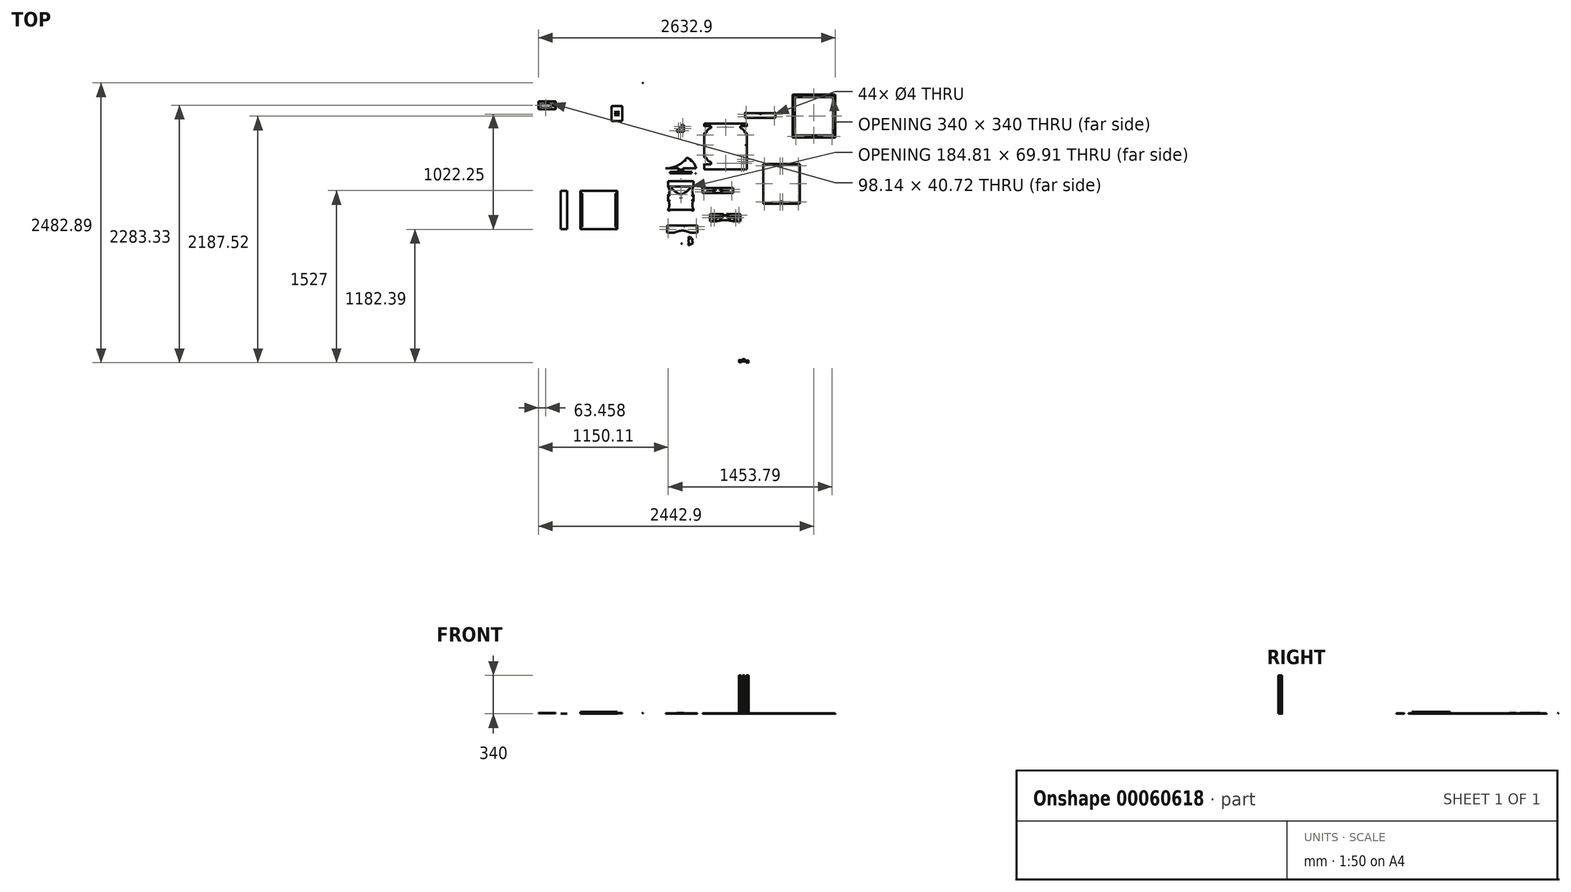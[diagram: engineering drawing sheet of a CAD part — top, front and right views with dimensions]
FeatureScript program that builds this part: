
annotation { "Feature Type Name" : "Feature", "Feature Type Description" : "" }
export const myFeature = defineFeature(function(context is Context, id is Id, definition is map)
    precondition{}
    {
        {
            var Q0;
            Q0=qCreatedBy(makeId("Top.planeOp"),FACE);
            var sketch = newSketch(context, id + "F0", { "sketchPlane" : qUnion([Q0])});
            skLineSegment(sketch, "E0", {"start": v(-196.4, -19.93) * mm, "end": v(-196.4, 30.07) * mm});
            skCircle(sketch, "E1", {"center": v(-187.75, 27.57) * mm, "radius": 2.75 * mm});
            skCircle(sketch, "E2", {"center": v(-187.75, -17.43) * mm, "radius": 2.75 * mm});
            skArc(sketch, "E3", {"start": v(-196.4, -19.93) * mm, "mid": v(-194.93, -23.47) * mm, "end": v(-191.4, -24.93) * mm});
            skArc(sketch, "E4", {"start": v(-191.4, 35.07) * mm, "mid": v(-194.93, 33.6) * mm, "end": v(-196.4, 30.07) * mm});
            skLineSegment(sketch, "E5", {"start": v(28.6, 30.07) * mm, "end": v(28.6, -19.93) * mm});
            skCircle(sketch, "E6", {"center": v(19.95, 27.57) * mm, "radius": 5.08 * mm});
            skCircle(sketch, "E7", {"center": v(19.95, -17.43) * mm, "radius": 5.08 * mm});
            skLineSegment(sketch, "E8.trimOffspring", {"start": v(14.88, 27.57) * mm, "end": v(19.95, 27.57) * mm});
            skPoint(sketch, "E9.visualSharp", {"position": v(28.6, 35.07) * mm});
            skArc(sketch, "E9.filletArc", {"start": v(28.6, 30.07) * mm, "mid": v(27.14, 33.6) * mm, "end": v(23.6, 35.07) * mm});
            skPoint(sketch, "E10.visualSharp", {"position": v(28.6, -24.93) * mm});
            skArc(sketch, "E10.filletArc", {"start": v(23.6, -24.93) * mm, "mid": v(27.14, -23.47) * mm, "end": v(28.6, -19.93) * mm});
            skCircle(sketch, "E11", {"center": v(-83.9, 5.07) * mm, "radius": 3.2 * mm});
            skLineSegment(sketch, "E12", {"start": v(-87.4, 19.55) * mm, "end": v(-80.33, 19.55) * mm});
            skLineSegment(sketch, "E13", {"start": v(-87.4, 21.55) * mm, "end": v(-80.33, 21.55) * mm});
            skLineSegment(sketch, "E14", {"start": v(-87.4, 23.86) * mm, "end": v(-80.32, 23.86) * mm});
            skLineSegment(sketch, "E15", {"start": v(-87.4, 25.86) * mm, "end": v(-80.32, 25.86) * mm});
            skLineSegment(sketch, "E16", {"start": v(-87.4, 27.93) * mm, "end": v(-80.32, 27.92) * mm});
            skLineSegment(sketch, "E17", {"start": v(-87.4, 31.34) * mm, "end": v(-80.31, 31.33) * mm});
            skLineSegment(sketch, "E18", {"start": v(-87.4, -9.95) * mm, "end": v(-80.38, -9.95) * mm});
            skLineSegment(sketch, "E19", {"start": v(-87.4, -11.95) * mm, "end": v(-80.38, -11.95) * mm});
            skLineSegment(sketch, "E20", {"start": v(-87.4, -16.14) * mm, "end": v(-80.39, -16.14) * mm});
            skLineSegment(sketch, "E21", {"start": v(-87.4, -14.14) * mm, "end": v(-80.39, -14.14) * mm});
            skLineSegment(sketch, "E22", {"start": v(-87.4, -21.89) * mm, "end": v(-80.4, -21.89) * mm});
            skLineSegment(sketch, "E23", {"start": v(-87.4, -18.45) * mm, "end": v(-80.4, -18.45) * mm});
            skLineSegment(sketch, "E24", {"start": v(-83.9, -21.89) * mm, "end": v(-80.4, -21.89) * mm});
            skLineSegment(sketch, "E25", {"start": v(-83.9, -21.89) * mm, "end": v(-87.4, -21.89) * mm});
            skLineSegment(sketch, "E26", {"start": v(-87.4, -21.89) * mm, "end": v(-87.4, -18.45) * mm});
            skLineSegment(sketch, "E27", {"start": v(-80.4, -21.89) * mm, "end": v(-80.4, -18.45) * mm});
            skLineSegment(sketch, "E28.trimOffspring", {"start": v(-87.4, 19.55) * mm, "end": v(-87.4, 21.55) * mm});
            skLineSegment(sketch, "E29.trimOffspring", {"start": v(-80.33, 19.55) * mm, "end": v(-80.33, 21.55) * mm});
            skLineSegment(sketch, "E30.trimOffspring", {"start": v(-80.32, 27.92) * mm, "end": v(-80.31, 31.34) * mm});
            skLineSegment(sketch, "E31.trimOffspring", {"start": v(-87.4, 27.93) * mm, "end": v(-87.4, 31.34) * mm});
            skLineSegment(sketch, "E32.trimOffspring", {"start": v(-87.4, 23.86) * mm, "end": v(-87.4, 25.86) * mm});
            skLineSegment(sketch, "E33.trimOffspring", {"start": v(-80.32, 23.86) * mm, "end": v(-80.32, 25.86) * mm});
            skLineSegment(sketch, "E34.trimOffspring", {"start": v(-87.4, -16.14) * mm, "end": v(-87.4, -14.14) * mm});
            skPoint(sketch, "E35.trimOffspring.end.orphan", {"position": v(-83.9, -24.93) * mm});
            skLineSegment(sketch, "E36.trimOffspring", {"start": v(-80.39, -16.14) * mm, "end": v(-80.39, -14.14) * mm});
            skLineSegment(sketch, "E37.trimOffspring", {"start": v(-87.4, -11.95) * mm, "end": v(-87.4, -9.95) * mm});
            skLineSegment(sketch, "E38.trimOffspring", {"start": v(-80.38, -11.95) * mm, "end": v(-80.38, -9.95) * mm});
            skCircle(sketch, "E39", {"center": v(-188.4, 109.57) * mm, "radius": 1.5 * mm});
            skCircle(sketch, "E40", {"center": v(20.6, 109.57) * mm, "radius": 1.5 * mm});
            skCircle(sketch, "E41", {"center": v(-188.4, -99.43) * mm, "radius": 1.5 * mm});
            skCircle(sketch, "E42", {"center": v(20.6, -99.43) * mm, "radius": 1.5 * mm});
            skLineSegment(sketch, "E43.MirrorCS", {"start": v(28.6, -19.93) * mm, "end": v(28.6, 30.07) * mm});
            skArc(sketch, "E44", {"start": v(-196.14, -94.85) * mm, "mid": v(-190.78, -108.11) * mm, "end": v(-179.4, -99.43) * mm});
            skArc(sketch, "E45", {"start": v(11.6, -99.43) * mm, "mid": v(22.98, -108.11) * mm, "end": v(28.34, -94.85) * mm});
            skArc(sketch, "E46", {"start": v(28.34, 104.98) * mm, "mid": v(22.98, 118.25) * mm, "end": v(11.6, 109.57) * mm});
            skArc(sketch, "E47", {"start": v(-179.4, 109.57) * mm, "mid": v(-190.78, 118.25) * mm, "end": v(-196.14, 104.98) * mm});
            skArc(sketch, "E48", {"start": v(-196.14, -94.85) * mm, "mid": v(-185.98, -60.42) * mm, "end": v(-191.4, -24.93) * mm});
            skArc(sketch, "E49", {"start": v(-83.9, -24.93) * mm, "mid": v(-137.85, -54.24) * mm, "end": v(-179.4, -99.43) * mm});
            skArc(sketch, "E50.MirrorCS", {"start": v(-83.9, -24.93) * mm, "mid": v(-29.95, -54.24) * mm, "end": v(11.6, -99.43) * mm});
            skArc(sketch, "E51.MirrorCS", {"start": v(28.34, -94.85) * mm, "mid": v(18.18, -60.42) * mm, "end": v(23.6, -24.93) * mm});
            skArc(sketch, "E52.MirrorCS", {"start": v(-83.9, 35.07) * mm, "mid": v(-137.85, 64.37) * mm, "end": v(-179.4, 109.57) * mm});
            skArc(sketch, "E53.MirrorCS", {"start": v(-196.14, 104.98) * mm, "mid": v(-185.98, 70.55) * mm, "end": v(-191.4, 35.07) * mm});
            skArc(sketch, "E54.MirrorCS", {"start": v(-83.9, 35.07) * mm, "mid": v(-29.95, 64.37) * mm, "end": v(11.6, 109.57) * mm});
            skArc(sketch, "E55.MirrorCS", {"start": v(28.34, 104.98) * mm, "mid": v(18.18, 70.55) * mm, "end": v(23.6, 35.07) * mm});
            skLineSegment(sketch, "E56.trimOffspring", {"start": v(-196.4, 5.07) * mm, "end": v(-227.61, 5.07) * mm});
            skLineSegment(sketch, "E57", {"start": v(-179.4, -99.43) * mm, "end": v(11.6, -99.43) * mm});
            skLineSegment(sketch, "E58", {"start": v(-179.4, 109.57) * mm, "end": v(11.6, 109.57) * mm});
            skLineSegment(sketch, "E59.bottom", {"start": v(-196.14, 104.98) * mm, "end": v(28.34, 104.98) * mm});
            skLineSegment(sketch, "E59.top", {"start": v(-196.14, 155.03) * mm, "end": v(28.34, 155.03) * mm});
            skLineSegment(sketch, "E59.left", {"start": v(-196.14, 104.98) * mm, "end": v(-196.14, 155.03) * mm});
            skLineSegment(sketch, "E59.right", {"start": v(28.34, 104.98) * mm, "end": v(28.34, 155.03) * mm});
            skSolve(sketch);
        }
        {
            var Q0;
            Q0=makeQuery(id+"F0.imprint","IMPRINT",FACE,{"disambiguationData":[TD([[makeQuery(id+"F0.imprint","IMPRINT",EDGE,{"derivedFrom":sQuery(id+"F0.wireOp",EDGE,"E0")}),-1.0]])]});
            var Q1;
            Q1=makeQuery(id+"F0.imprint","IMPRINT",FACE,{"disambiguationData":[TD([[makeQuery(id+"F0.imprint","IMPRINT",EDGE,{"derivedFrom":sQuery(id+"F0.wireOp",EDGE,"E23")}),-1.0]])]});
            var Q2;
            Q2=makeQuery(id+"F0.imprint","IMPRINT",FACE,{"disambiguationData":[TD([[makeQuery(id+"F0.imprint","IMPRINT",EDGE,{"derivedFrom":sQuery(id+"F0.wireOp",EDGE,"E49")}),1.0]])]});
            var Q3;
            Q3=makeQuery(id+"F0.imprint","IMPRINT",FACE,{"disambiguationData":[TD([[makeQuery(id+"F0.imprint","IMPRINT",EDGE,{"derivedFrom":sQuery(id+"F0.wireOp",EDGE,"E18")}),-1.0]])]});
            var Q4;
            Q4=makeQuery(id+"F0.imprint","IMPRINT",FACE,{"disambiguationData":[TD([[makeQuery(id+"F0.imprint","IMPRINT",EDGE,{"derivedFrom":sQuery(id+"F0.wireOp",EDGE,"E20")}),1.0]])]});
            var Q5;
            Q5=makeQuery(id+"F0.imprint","IMPRINT",FACE,{"disambiguationData":[TD([[makeQuery(id+"F0.imprint","IMPRINT",EDGE,{"derivedFrom":sQuery(id+"F0.wireOp",EDGE,"E52.MirrorCS")}),-1.0]])]});
            var Q6;
            Q6=makeQuery(id+"F0.imprint","IMPRINT",FACE,{"disambiguationData":[TD([[makeQuery(id+"F0.imprint","IMPRINT",EDGE,{"derivedFrom":sQuery(id+"F0.wireOp",EDGE,"E12")}),1.0]])]});
            var Q7;
            Q7=makeQuery(id+"F0.imprint","IMPRINT",FACE,{"disambiguationData":[TD([[makeQuery(id+"F0.imprint","IMPRINT",EDGE,{"derivedFrom":sQuery(id+"F0.wireOp",EDGE,"E14")}),1.0]])]});
            var Q8;
            {var subQ2=sQuery(id+"F0.wireOp",EDGE,"E16");Q8=makeQuery(id+"F0.imprint","IMPRINT",FACE,{"disambiguationData":[TD([[makeQuery(id+"F0.imprint","IMPRINT",EDGE,{"derivedFrom":subQ2}),1.0]])]});}
            var Q9;
            {var subQ7=sQuery(id+"F0.wireOp",EDGE,"E58");Q9=makeQuery(id+"F0.imprint","IMPRINT",FACE,{"disambiguationData":[TD([[makeQuery(id+"F0.imprint","IMPRINT",EDGE,{"derivedFrom":subQ7}),1.0]])]});}
            var Q10;
            Q10=makeQuery(id+"F0.imprint","IMPRINT",FACE,{"disambiguationData":[TD([[makeQuery(id+"F0.imprint","IMPRINT",EDGE,{"derivedFrom":sQuery(id+"F0.wireOp",EDGE,"E40")}),-1.0]])]});
            var Q11;
            Q11=makeQuery(id+"F0.imprint","IMPRINT",FACE,{"disambiguationData":[TD([[makeQuery(id+"F0.imprint","IMPRINT",EDGE,{"derivedFrom":sQuery(id+"F0.wireOp",EDGE,"E39")}),-1.0]])]});
            var Q12;
            {var subQ5=sQuery(id+"F0.wireOp",EDGE,"E58");Q12=makeQuery(id+"F0.imprint","IMPRINT",FACE,{"disambiguationData":[TD([[makeQuery(id+"F0.imprint","IMPRINT",EDGE,{"derivedFrom":subQ5}),-1.0]])]});}
            extrude(context, id + "F1", {"entities" : qUnion([Q0, Q1, Q2, Q3, Q4, Q5, Q6, Q7, Q8, Q9, Q10, Q11, Q12]), "depth" : 4 * mm});
        }
        {
            var Q0;
            Q0=qCreatedBy(makeId("Top.planeOp"),FACE);
            var sketch = newSketch(context, id + "F2", { "sketchPlane" : qUnion([Q0])});
            skLineSegment(sketch, "E60", {"start": v(-104.69, 266.67) * mm, "end": v(-62.63, 266.67) * mm});
            skLineSegment(sketch, "E61", {"start": v(-62.63, 266.67) * mm, "end": v(-62.63, 266.67) * mm});
            skLineSegment(sketch, "E62", {"start": v(-62.63, 266.67) * mm, "end": v(51.38, 266.67) * mm});
            skLineSegment(sketch, "E63", {"start": v(51.38, 266.67) * mm, "end": v(51.38, 224.88) * mm});
            skLineSegment(sketch, "E64", {"start": v(51.38, 224.88) * mm, "end": v(41.38, 224.88) * mm});
            skLineSegment(sketch, "E65", {"start": v(41.38, 224.88) * mm, "end": v(51.38, 224.88) * mm});
            skLineSegment(sketch, "E66.bottom", {"start": v(-104.69, 266.67) * mm, "end": v(-62.62, 266.67) * mm});
            skLineSegment(sketch, "E66.right", {"start": v(-62.62, 266.67) * mm, "end": v(-62.62, 224.88) * mm});
            skLineSegment(sketch, "E67", {"start": v(-104.69, 224.88) * mm, "end": v(-62.62, 224.88) * mm});
            skLineSegment(sketch, "E68", {"start": v(-62.62, 224.88) * mm, "end": v(41.38, 224.88) * mm});
            skLineSegment(sketch, "E69", {"start": v(-104.69, 224.88) * mm, "end": v(-104.69, 266.67) * mm});
            skCircle(sketch, "E70", {"center": v(41.38, 258.88) * mm, "radius": 2 * mm});
            skCircle(sketch, "E71", {"center": v(41.38, 234.88) * mm, "radius": 2 * mm});
            skCircle(sketch, "E72", {"center": v(-83.65, 245.28) * mm, "radius": 11.05 * mm});
            skCircle(sketch, "E73", {"center": v(-99.2, 229.73) * mm, "radius": 1.65 * mm});
            skCircle(sketch, "E74", {"center": v(-68.1, 229.79) * mm, "radius": 1.65 * mm});
            skCircle(sketch, "E75", {"center": v(-99.2, 260.83) * mm, "radius": 1.65 * mm});
            skCircle(sketch, "E76", {"center": v(-68.1, 261) * mm, "radius": 1.65 * mm});
            skLineSegment(sketch, "E77", {"start": v(-83.66, 224.88) * mm, "end": v(-83.66, 266.67) * mm});
            skLineSegment(sketch, "E78.MirrorCS", {"start": v(-104.69, 224.88) * mm, "end": v(-208.69, 224.88) * mm});
            skLineSegment(sketch, "E79.MirrorCS", {"start": v(-104.69, 266.67) * mm, "end": v(-218.69, 266.67) * mm});
            skLineSegment(sketch, "E80.MirrorCS", {"start": v(-218.69, 266.67) * mm, "end": v(-218.69, 224.88) * mm});
            skLineSegment(sketch, "E81.MirrorCS", {"start": v(-208.69, 224.88) * mm, "end": v(-210.69, 224.88) * mm});
            skCircle(sketch, "E82.MirrorC", {"center": v(-208.69, 234.88) * mm, "radius": 2 * mm});
            skCircle(sketch, "E83.MirrorC", {"center": v(-208.69, 258.88) * mm, "radius": 2 * mm});
            skLineSegment(sketch, "E84.bottom", {"start": v(-83.66, 224.88) * mm, "end": v(-181, 224.88) * mm});
            skLineSegment(sketch, "E84.top", {"start": v(-83.66, 237.25) * mm, "end": v(-181, 237.25) * mm});
            skLineSegment(sketch, "E84.left", {"start": v(-83.66, 224.88) * mm, "end": v(-83.66, 237.25) * mm});
            skLineSegment(sketch, "E84.right", {"start": v(-181, 224.88) * mm, "end": v(-181, 237.25) * mm});
            skLineSegment(sketch, "E85.MirrorCS", {"start": v(-83.66, 237.25) * mm, "end": v(13.7, 237.25) * mm});
            skLineSegment(sketch, "E86.MirrorCS", {"start": v(13.7, 224.88) * mm, "end": v(13.7, 237.25) * mm});
            skCircle(sketch, "E87", {"center": v(3.35, 260.88) * mm, "radius": 1.5 * mm});
            skCircle(sketch, "E88", {"center": v(-44.47, 253.5) * mm, "radius": 1.5 * mm});
            skCircle(sketch, "E89", {"center": v(-44.78, 334.21) * mm, "radius": 1.5 * mm});
            skCircle(sketch, "E90", {"center": v(3.26, 334.22) * mm, "radius": 1.5 * mm});
            skArc(sketch, "E91", {"start": v(51.38, 266.67) * mm, "mid": v(26.53, 319.96) * mm, "end": v(-18.2, 358.13) * mm});
            skArc(sketch, "E92", {"start": v(-218.69, 266.67) * mm, "mid": v(-117.85, 289.71) * mm, "end": v(-37.02, 354.25) * mm});
            skArc(sketch, "E93.filletArc", {"start": v(-18.2, 358.13) * mm, "mid": v(-28.3, 359.6) * mm, "end": v(-37.02, 354.25) * mm});
            skLineSegment(sketch, "E94", {"start": v(-218.69, 224.88) * mm, "end": v(-218.69, 220.88) * mm});
            skLineSegment(sketch, "E95", {"start": v(-218.69, 220.88) * mm, "end": v(-210.69, 220.88) * mm});
            skLineSegment(sketch, "E96", {"start": v(-210.69, 220.88) * mm, "end": v(-210.69, 224.88) * mm});
            skLineSegment(sketch, "E97.MirrorCS", {"start": v(51.38, 224.88) * mm, "end": v(51.38, 220.88) * mm});
            skLineSegment(sketch, "E98.MirrorCS", {"start": v(43.38, 220.88) * mm, "end": v(43.38, 224.88) * mm});
            skLineSegment(sketch, "E99.MirrorCS", {"start": v(51.38, 220.88) * mm, "end": v(43.38, 220.88) * mm});
            skPoint(sketch, "E100.orphan", {"position": v(-218.69, 224.88) * mm});
            skSolve(sketch);
        }
        {
            var Q0;
            {var subQ8=sQuery(id+"F2.wireOp",EDGE,"E62");Q0=makeQuery(id+"F2.imprint","IMPRINT",FACE,{"disambiguationData":[TD([[makeQuery(id+"F2.imprint","IMPRINT",EDGE,{"derivedFrom":subQ8}),1.0]])]});}
            var Q1;
            Q1=makeQuery(id+"F2.imprint","IMPRINT",FACE,{"disambiguationData":[TD([[makeQuery(id+"F2.imprint","IMPRINT",EDGE,{"derivedFrom":sQuery(id+"F2.wireOp",EDGE,"E78.MirrorCS")}),-1.0]])]});
            var Q2;
            Q2=makeQuery(id+"F2.imprint","IMPRINT",FACE,{"disambiguationData":[TD([[makeQuery(id+"F2.imprint","IMPRINT",EDGE,{"derivedFrom":sQuery(id+"F2.wireOp",EDGE,"E73")}),-1.0]])]});
            var Q3;
            Q3=makeQuery(id+"F2.imprint","IMPRINT",FACE,{"disambiguationData":[TD([[makeQuery(id+"F2.imprint","IMPRINT",EDGE,{"derivedFrom":sQuery(id+"F2.wireOp",EDGE,"E74")}),-1.0]])]});
            var Q4;
            {var subQ1=sQuery(id+"F2.wireOp",EDGE,"E97.MirrorCS");Q4=makeQuery(id+"F2.imprint","IMPRINT",FACE,{"disambiguationData":[TD([[makeQuery(id+"F2.imprint","IMPRINT",EDGE,{"derivedFrom":subQ1}),-1.0]])]});}
            var Q5;
            Q5=makeQuery(id+"F2.imprint","IMPRINT",FACE,{"disambiguationData":[TD([[makeQuery(id+"F2.imprint","IMPRINT",EDGE,{"derivedFrom":sQuery(id+"F2.wireOp",EDGE,"E75")}),-1.0]])]});
            var Q6;
            Q6=makeQuery(id+"F2.imprint","IMPRINT",FACE,{"disambiguationData":[TD([[makeQuery(id+"F2.imprint","IMPRINT",EDGE,{"derivedFrom":sQuery(id+"F2.wireOp",EDGE,"E76")}),-1.0]])]});
            var Q7;
            {var subQ5=sQuery(id+"F2.wireOp",EDGE,"E86.MirrorCS");Q7=makeQuery(id+"F2.imprint","IMPRINT",FACE,{"disambiguationData":[TD([[makeQuery(id+"F2.imprint","IMPRINT",EDGE,{"derivedFrom":subQ5}),1.0]])]});}
            var Q8;
            {var subQ5=sQuery(id+"F2.wireOp",EDGE,"E84.right");Q8=makeQuery(id+"F2.imprint","IMPRINT",FACE,{"disambiguationData":[TD([[makeQuery(id+"F2.imprint","IMPRINT",EDGE,{"derivedFrom":subQ5}),-1.0]])]});}
            var Q9;
            {var subQ7=sQuery(id+"F2.wireOp",EDGE,"E62");Q9=makeQuery(id+"F2.imprint","IMPRINT",FACE,{"disambiguationData":[TD([[makeQuery(id+"F2.imprint","IMPRINT",EDGE,{"derivedFrom":subQ7}),-1.0]])]});}
            extrude(context, id + "F3", {"entities" : qUnion([Q0, Q1, Q2, Q3, Q4, Q5, Q6, Q7, Q8, Q9]), "depth" : 4 * mm});
        }
        {
            var Q0;
            Q0=qCreatedBy(makeId("Top.planeOp"),FACE);
            var sketch = newSketch(context, id + "F4", { "sketchPlane" : qUnion([Q0])});
            skLineSegment(sketch, "E101", {"start": v(600.2, 758.38) * mm, "end": v(642.2, 758.38) * mm});
            skLineSegment(sketch, "E102", {"start": v(642.2, 758.38) * mm, "end": v(642.2, 758.38) * mm});
            skLineSegment(sketch, "E103", {"start": v(642.2, 758.38) * mm, "end": v(748.23, 758.38) * mm});
            skLineSegment(sketch, "E104", {"start": v(756.23, 758.38) * mm, "end": v(756.23, 716.59) * mm});
            skLineSegment(sketch, "E105", {"start": v(756.23, 716.59) * mm, "end": v(746.23, 716.59) * mm});
            skLineSegment(sketch, "E106", {"start": v(746.23, 716.59) * mm, "end": v(756.23, 716.59) * mm});
            skLineSegment(sketch, "E107.bottom", {"start": v(600.2, 758.38) * mm, "end": v(642.26, 758.38) * mm});
            skLineSegment(sketch, "E107.right", {"start": v(642.26, 758.38) * mm, "end": v(642.26, 716.59) * mm});
            skLineSegment(sketch, "E108", {"start": v(600.2, 716.59) * mm, "end": v(642.26, 716.59) * mm});
            skLineSegment(sketch, "E109", {"start": v(642.26, 716.59) * mm, "end": v(746.23, 716.59) * mm});
            skLineSegment(sketch, "E110", {"start": v(600.2, 716.59) * mm, "end": v(600.2, 758.38) * mm});
            skCircle(sketch, "E111", {"center": v(746.23, 747.66) * mm, "radius": 2 * mm});
            skCircle(sketch, "E112", {"center": v(746.23, 725.6) * mm, "radius": 2 * mm});
            skLineSegment(sketch, "E113", {"start": v(621.23, 716.59) * mm, "end": v(621.23, 758.38) * mm});
            skLineSegment(sketch, "E114.MirrorCS", {"start": v(600.2, 716.59) * mm, "end": v(496.23, 716.59) * mm});
            skLineSegment(sketch, "E115.MirrorCS", {"start": v(600.26, 758.38) * mm, "end": v(494.23, 758.38) * mm});
            skLineSegment(sketch, "E116.MirrorCS", {"start": v(486.23, 758.38) * mm, "end": v(486.23, 716.59) * mm});
            skLineSegment(sketch, "E117.MirrorCS", {"start": v(496.23, 716.59) * mm, "end": v(486.23, 716.59) * mm});
            skCircle(sketch, "E118.MirrorC", {"center": v(496.23, 725.6) * mm, "radius": 2 * mm});
            skCircle(sketch, "E119.MirrorC", {"center": v(496.23, 747.66) * mm, "radius": 2 * mm});
            skCircle(sketch, "E120", {"center": v(621.23, 746.98) * mm, "radius": 1.5 * mm});
            skPoint(sketch, "E121", {"position": v(494.23, 758.38) * mm});
            skPoint(sketch, "E122", {"position": v(735, 758.38) * mm});
            skLineSegment(sketch, "E123", {"start": v(486.23, 758.38) * mm, "end": v(486.23, 762.38) * mm});
            skLineSegment(sketch, "E124", {"start": v(486.23, 762.38) * mm, "end": v(494.23, 762.38) * mm});
            skLineSegment(sketch, "E125", {"start": v(494.23, 762.38) * mm, "end": v(494.23, 758.38) * mm});
            skLineSegment(sketch, "E126.MirrorCS", {"start": v(756.23, 762.38) * mm, "end": v(748.23, 762.38) * mm});
            skLineSegment(sketch, "E127.MirrorCS", {"start": v(756.23, 758.38) * mm, "end": v(756.23, 762.38) * mm});
            skLineSegment(sketch, "E128.MirrorCS", {"start": v(748.23, 762.38) * mm, "end": v(748.23, 758.38) * mm});
            skSolve(sketch);
        }
        {
            var Q0;
            Q0=makeQuery(id+"F4.imprint","IMPRINT",FACE,{"disambiguationData":[TD([[makeQuery(id+"F4.imprint","IMPRINT",EDGE,{"derivedFrom":sQuery(id+"F4.wireOp",EDGE,"E103")}),-1.0]])]});
            var Q1;
            {var subQ8=sQuery(id+"F4.wireOp",EDGE,"E107.right");Q1=makeQuery(id+"F4.imprint","IMPRINT",FACE,{"disambiguationData":[TD([[makeQuery(id+"F4.imprint","IMPRINT",EDGE,{"derivedFrom":subQ8}),-1.0]])]});}
            var Q2;
            {var subQ5=sQuery(id+"F4.wireOp",EDGE,"E110");Q2=makeQuery(id+"F4.imprint","IMPRINT",FACE,{"disambiguationData":[TD([[makeQuery(id+"F4.imprint","IMPRINT",EDGE,{"derivedFrom":subQ5}),-1.0]])]});}
            var Q3;
            {var subQ2=sQuery(id+"F4.wireOp",EDGE,"E110");Q3=makeQuery(id+"F4.imprint","IMPRINT",FACE,{"disambiguationData":[TD([[makeQuery(id+"F4.imprint","IMPRINT",EDGE,{"derivedFrom":subQ2}),1.0]])]});}
            extrude(context, id + "F5", {"entities" : qUnion([Q0, Q1, Q2, Q3]), "depth" : 4 * mm});
        }
        {
            var Q0;
            Q0=qCreatedBy(makeId("Top.planeOp"),FACE);
            var sketch = newSketch(context, id + "F6", { "sketchPlane" : qUnion([Q0])});
            skLineSegment(sketch, "E129", {"start": v(63.81, -240.59) * mm, "end": v(63.81, -260.59) * mm});
            skCircle(sketch, "E130", {"center": v(53.81, -250.59) * mm, "radius": 2 * mm});
            skCircle(sketch, "E131.MirrorC", {"center": v(-196.26, -250.59) * mm, "radius": 2 * mm});
            skCircle(sketch, "E132", {"center": v(-196.26, -274.59) * mm, "radius": 2 * mm});
            skCircle(sketch, "E133.MirrorC", {"center": v(53.81, -274.59) * mm, "radius": 2 * mm});
            skCircle(sketch, "E134", {"center": v(-76.65, -399.92) * mm, "radius": 1.75 * mm});
            skCircle(sketch, "E135", {"center": v(-76.65, -349.92) * mm, "radius": 1.75 * mm});
            skCircle(sketch, "E136", {"center": v(-221.83, -399.92) * mm, "radius": 1.75 * mm});
            skCircle(sketch, "E137", {"center": v(-221.65, -349.97) * mm, "radius": 1.75 * mm});
            skPoint(sketch, "E138", {"position": v(63.81, -264.59) * mm});
            skLineSegment(sketch, "E139", {"start": v(63.81, -264.59) * mm, "end": v(55.81, -264.59) * mm});
            skLineSegment(sketch, "E140", {"start": v(55.81, -264.59) * mm, "end": v(55.81, -260.59) * mm});
            skLineSegment(sketch, "E141", {"start": v(55.81, -260.59) * mm, "end": v(63.81, -260.59) * mm});
            skLineSegment(sketch, "E142.MirrorCS", {"start": v(-206.26, -264.59) * mm, "end": v(-198.26, -264.59) * mm});
            skLineSegment(sketch, "E143.MirrorCS", {"start": v(-198.26, -264.59) * mm, "end": v(-198.26, -260.59) * mm});
            skLineSegment(sketch, "E144.MirrorCS", {"start": v(-198.26, -260.59) * mm, "end": v(-206.26, -260.59) * mm});
            skCircle(sketch, "E145.MirrorC", {"center": v(-86.96, -378.05) * mm, "radius": 10 * mm});
            skLineSegment(sketch, "E146.trimOffspring", {"start": v(-206.26, -264.59) * mm, "end": v(-206.26, -304.59) * mm});
            skLineSegment(sketch, "E147.trimOffspring", {"start": v(63.81, -264.59) * mm, "end": v(63.81, -304.59) * mm});
            skLineSegment(sketch, "E148", {"start": v(-206.26, -260.59) * mm, "end": v(-206.26, -240.59) * mm});
            skLineSegment(sketch, "E149", {"start": v(63.81, -240.59) * mm, "end": v(-206.26, -240.59) * mm});
            skLineSegment(sketch, "E150", {"start": v(-206.26, -304.59) * mm, "end": v(-144.26, -304.59) * mm});
            skLineSegment(sketch, "E151", {"start": v(1.81, -304.59) * mm, "end": v(63.81, -304.59) * mm});
            skLineSegment(sketch, "E152.bottom", {"start": v(-230, -345.8) * mm, "end": v(-68.48, -345.8) * mm});
            skLineSegment(sketch, "E152.top", {"start": v(-230, -417.83) * mm, "end": v(-68.48, -417.83) * mm});
            skLineSegment(sketch, "E152.right", {"start": v(-68.48, -345.8) * mm, "end": v(-68.48, -356.82) * mm});
            skCircle(sketch, "E153", {"center": v(-54.27, -294.37) * mm, "radius": 1.75 * mm});
            skCircle(sketch, "E154", {"center": v(-54.27, -244.37) * mm, "radius": 1.75 * mm});
            skArc(sketch, "E155", {"start": v(1.81, -304.59) * mm, "mid": v(-71.22, -285.2) * mm, "end": v(-144.26, -304.59) * mm});
            skLineSegment(sketch, "E156", {"start": v(-68.48, -399.92) * mm, "end": v(-64.48, -399.92) * mm});
            skLineSegment(sketch, "E157", {"start": v(-68.48, -385.74) * mm, "end": v(-64.48, -385.74) * mm});
            skLineSegment(sketch, "E158", {"start": v(-68.48, -356.82) * mm, "end": v(-64.48, -356.82) * mm});
            skLineSegment(sketch, "E159", {"start": v(-68.48, -370.31) * mm, "end": v(-64.48, -370.31) * mm});
            skLineSegment(sketch, "E160.trimOffspring", {"start": v(-68.48, -370.31) * mm, "end": v(-68.48, -385.74) * mm});
            skLineSegment(sketch, "E161.trimOffspring", {"start": v(-68.48, -399.92) * mm, "end": v(-68.48, -417.83) * mm});
            skLineSegment(sketch, "E162.MirrorCS", {"start": v(-12.72, -366.04) * mm, "end": v(-12.72, -352.54) * mm});
            skLineSegment(sketch, "E163.MirrorCS", {"start": v(-16.72, -395.64) * mm, "end": v(-12.72, -395.64) * mm});
            skLineSegment(sketch, "E164.MirrorCS", {"start": v(-12.72, -395.64) * mm, "end": v(-12.72, -381.46) * mm});
            skLineSegment(sketch, "E165.MirrorCS", {"start": v(-16.72, -381.46) * mm, "end": v(-12.72, -381.46) * mm});
            skLineSegment(sketch, "E166", {"start": v(-12.72, -366.04) * mm, "end": v(-16.72, -366.04) * mm});
            skLineSegment(sketch, "E167", {"start": v(-12.72, -352.54) * mm, "end": v(-16.72, -352.54) * mm});
            skLineSegment(sketch, "E168", {"start": v(-16.72, -352.54) * mm, "end": v(-12.72, -352.54) * mm});
            skLineSegment(sketch, "E169", {"start": v(-16.72, -408.89) * mm, "end": v(-16.72, -395.64) * mm});
            skLineSegment(sketch, "E170", {"start": v(-12.72, -340.89) * mm, "end": v(-16.72, -340.89) * mm});
            skLineSegment(sketch, "E171", {"start": v(-16.72, -381.46) * mm, "end": v(-16.72, -366.04) * mm});
            skLineSegment(sketch, "E172", {"start": v(-16.72, -352.54) * mm, "end": v(-16.72, -340.89) * mm});
            skArc(sketch, "E173", {"start": v(-64.48, -415.8) * mm, "mid": v(-44.88, -381.81) * mm, "end": v(-64.48, -347.82) * mm});
            skLineSegment(sketch, "E174", {"start": v(-64.48, -399.92) * mm, "end": v(-64.48, -415.8) * mm});
            skLineSegment(sketch, "E175", {"start": v(-64.48, -385.74) * mm, "end": v(-64.48, -370.31) * mm});
            skLineSegment(sketch, "E176.trimOffspring", {"start": v(-64.48, -356.82) * mm, "end": v(-64.48, -347.82) * mm});
            skLineSegment(sketch, "E177", {"start": v(-221.83, -399.92) * mm, "end": v(-76.65, -399.92) * mm, "construction": true});
            skLineSegment(sketch, "E178", {"start": v(-149.24, -399.92) * mm, "end": v(-149.24, -377.49) * mm, "construction": true});
            skLineSegment(sketch, "E179.MirrorCS", {"start": v(-230, -399.92) * mm, "end": v(-230, -417.83) * mm});
            skLineSegment(sketch, "E180.MirrorCS", {"start": v(-234, -399.92) * mm, "end": v(-234, -415.8) * mm});
            skLineSegment(sketch, "E181.MirrorCS", {"start": v(-230, -399.92) * mm, "end": v(-234, -399.92) * mm});
            skLineSegment(sketch, "E182.MirrorCS", {"start": v(-230, -370.31) * mm, "end": v(-230, -385.74) * mm});
            skLineSegment(sketch, "E183.MirrorCS", {"start": v(-234, -385.74) * mm, "end": v(-234, -370.31) * mm});
            skLineSegment(sketch, "E184.MirrorCS", {"start": v(-230, -370.31) * mm, "end": v(-234, -370.31) * mm});
            skLineSegment(sketch, "E185.MirrorCS", {"start": v(-230, -345.8) * mm, "end": v(-230, -356.82) * mm});
            skLineSegment(sketch, "E186.MirrorCS", {"start": v(-234, -356.82) * mm, "end": v(-234, -347.82) * mm});
            skArc(sketch, "E187.MirrorCS", {"start": v(-234, -415.8) * mm, "mid": v(-253.6, -381.81) * mm, "end": v(-234, -347.82) * mm});
            skLineSegment(sketch, "E188.MirrorCS", {"start": v(-230, -385.74) * mm, "end": v(-234, -385.74) * mm});
            skLineSegment(sketch, "E189.MirrorCS", {"start": v(-230, -356.82) * mm, "end": v(-234, -356.82) * mm});
            skLineSegment(sketch, "E190", {"start": v(-1.23, -340.89) * mm, "end": v(-12.72, -340.89) * mm});
            skLineSegment(sketch, "E191", {"start": v(-16.72, -395.64) * mm, "end": v(-16.72, -413.55) * mm});
            skLineSegment(sketch, "E192", {"start": v(-12.72, -413.55) * mm, "end": v(-16.72, -413.55) * mm});
            skLineSegment(sketch, "E193", {"start": v(-12.72, -413.55) * mm, "end": v(25.7, -394.12) * mm});
            skPoint(sketch, "E194.start.orphan", {"position": v(-1.23, -340.89) * mm});
            skLineSegment(sketch, "E195", {"start": v(-1.23, -340.89) * mm, "end": v(7.72, -358.58) * mm});
            skLineSegment(sketch, "E196", {"start": v(15.8, -365.7) * mm, "end": v(11.29, -356.78) * mm});
            skLineSegment(sketch, "E197", {"start": v(11.29, -356.78) * mm, "end": v(7.72, -358.58) * mm});
            skLineSegment(sketch, "E198", {"start": v(15.8, -365.7) * mm, "end": v(20.31, -374.62) * mm});
            skLineSegment(sketch, "E199", {"start": v(20.31, -374.62) * mm, "end": v(16.74, -376.43) * mm});
            skLineSegment(sketch, "E200.trimOffspring", {"start": v(16.74, -376.43) * mm, "end": v(25.7, -394.12) * mm});
            skLineSegment(sketch, "E201", {"start": v(-64.48, -385.74) * mm, "end": v(-56.77, -385.74) * mm, "construction": true});
            skArc(sketch, "E202", {"start": v(-52.77, -381.74) * mm, "mid": v(-54.77, -379.74) * mm, "end": v(-56.77, -381.74) * mm});
            skArc(sketch, "E203.MirrorC", {"start": v(-52.77, -385.74) * mm, "mid": v(-54.77, -387.74) * mm, "end": v(-56.77, -385.74) * mm});
            skLineSegment(sketch, "E204", {"start": v(-52.77, -385.74) * mm, "end": v(-52.77, -381.74) * mm});
            skLineSegment(sketch, "E205", {"start": v(-56.77, -381.74) * mm, "end": v(-56.77, -385.74) * mm});
            skArc(sketch, "E206.MirrorCS", {"start": v(-245.71, -385.74) * mm, "mid": v(-243.71, -387.74) * mm, "end": v(-241.71, -385.74) * mm});
            skLineSegment(sketch, "E207.MirrorCS", {"start": v(-245.71, -385.74) * mm, "end": v(-245.71, -381.74) * mm});
            skArc(sketch, "E208.MirrorCS", {"start": v(-245.71, -381.74) * mm, "mid": v(-243.71, -379.74) * mm, "end": v(-241.71, -381.74) * mm});
            skLineSegment(sketch, "E209.MirrorCS", {"start": v(-241.71, -381.74) * mm, "end": v(-241.71, -385.74) * mm});
            skPoint(sketch, "E210", {"position": v(-54.75, -385.74) * mm});
            skLineSegment(sketch, "E211.bottom", {"start": v(-210.56, -361.3) * mm, "end": v(-112.3, -361.3) * mm});
            skLineSegment(sketch, "E211.top", {"start": v(-210.56, -402.02) * mm, "end": v(-112.3, -402.02) * mm});
            skLineSegment(sketch, "E211.left", {"start": v(-210.56, -361.3) * mm, "end": v(-210.56, -402.02) * mm});
            skLineSegment(sketch, "E211.right", {"start": v(-112.3, -361.3) * mm, "end": v(-112.3, -402.02) * mm});
            skSolve(sketch);
        }
        {
            var Q0;
            Q0=makeQuery(id+"F6.imprint","IMPRINT",FACE,{"disambiguationData":[TD([[makeQuery(id+"F6.imprint","IMPRINT",EDGE,{"derivedFrom":sQuery(id+"F6.wireOp",EDGE,"E129")}),-1.0]])]});
            var Q1;
            Q1=makeQuery(id+"F6.imprint","IMPRINT",FACE,{"disambiguationData":[TD([[makeQuery(id+"F6.imprint","IMPRINT",EDGE,{"derivedFrom":sQuery(id+"F6.wireOp",EDGE,"E134")}),1.0]])]});
            var Q2;
            Q2=makeQuery(id+"F6.imprint","IMPRINT",FACE,{"disambiguationData":[TD([[makeQuery(id+"F6.imprint","IMPRINT",EDGE,{"derivedFrom":sQuery(id+"F6.wireOp",EDGE,"2918f89a-1ed2-4754-b867-7cf13f7856ee")}),-1.0]])]});
            var Q3;
            Q3=makeQuery(id+"F6.imprint","IMPRINT",FACE,{"disambiguationData":[TD([[makeQuery(id+"F6.imprint","IMPRINT",EDGE,{"derivedFrom":sQuery(id+"F6.wireOp",EDGE,"2918f89a-1ed2-4754-b867-7cf13f7856ee")}),1.0]])]});
            var Q4;
            Q4=makeQuery(id+"F6.imprint","IMPRINT",FACE,{"disambiguationData":[TD([[makeQuery(id+"F6.imprint","IMPRINT",EDGE,{"derivedFrom":sQuery(id+"F6.wireOp",EDGE,"E162.MirrorCS")}),-1.0]])]});
            extrude(context, id + "F7", {"entities" : qUnion([Q0, Q1, Q2, Q3, Q4]), "depth" : 4 * mm});
        }
        {
            var Q0;
            Q0=qCreatedBy(makeId("Top.planeOp"),FACE);
            var sketch = newSketch(context, id + "F8", { "sketchPlane" : qUnion([Q0])});
            skLineSegment(sketch, "E212.MirrorCS", {"start": v(234.93, -201.78) * mm, "end": v(182.93, -201.78) * mm});
            skLineSegment(sketch, "E213.MirrorCS", {"start": v(294.45, -137.78) * mm, "end": v(172.93, -137.78) * mm});
            skCircle(sketch, "E214", {"center": v(182.93, -171.78) * mm, "radius": 2 * mm});
            skArc(sketch, "E215", {"start": v(381, -201.78) * mm, "mid": v(307.96, -191.74) * mm, "end": v(234.93, -201.78) * mm});
            skLineSegment(sketch, "E216", {"start": v(321.48, -137.78) * mm, "end": v(443, -137.78) * mm});
            skLineSegment(sketch, "E217", {"start": v(381, -201.78) * mm, "end": v(433, -201.78) * mm});
            skLineSegment(sketch, "E218.MirrorCS", {"start": v(172.93, -137.78) * mm, "end": v(172.93, -157.78) * mm});
            skCircle(sketch, "E219.MirrorC", {"center": v(433, -171.78) * mm, "radius": 2 * mm});
            skLineSegment(sketch, "E220.MirrorCS", {"start": v(182.93, -201.78) * mm, "end": v(172.93, -201.78) * mm});
            skCircle(sketch, "E221.MirrorC", {"center": v(182.93, -147.78) * mm, "radius": 2 * mm});
            skLineSegment(sketch, "E222", {"start": v(443, -137.78) * mm, "end": v(443, -157.78) * mm});
            skCircle(sketch, "E223", {"center": v(433, -147.78) * mm, "radius": 2 * mm});
            skLineSegment(sketch, "E224", {"start": v(433, -201.78) * mm, "end": v(443, -201.78) * mm});
            skLineSegment(sketch, "E225", {"start": v(443, -201.78) * mm, "end": v(433, -201.78) * mm});
            skLineSegment(sketch, "E226", {"start": v(182.93, -201.78) * mm, "end": v(192.93, -201.78) * mm});
            skLineSegment(sketch, "E227.0", {"start": v(217.13, -158.47) * mm, "end": v(213.2, -166.38) * mm});
            skLineSegment(sketch, "E227.1", {"start": v(213.2, -166.38) * mm, "end": v(204.38, -166.93) * mm});
            skLineSegment(sketch, "E227.2", {"start": v(204.38, -166.93) * mm, "end": v(199.5, -159.57) * mm});
            skLineSegment(sketch, "E227.3", {"start": v(199.5, -159.57) * mm, "end": v(203.44, -151.66) * mm});
            skLineSegment(sketch, "E227.4", {"start": v(203.44, -151.66) * mm, "end": v(212.25, -151.11) * mm});
            skLineSegment(sketch, "E227.5", {"start": v(212.25, -151.11) * mm, "end": v(217.13, -158.47) * mm});
            skPoint(sketch, "E227.0.midPoint", {"position": v(215.17, -162.43) * mm});
            skPoint(sketch, "E228.0.midPoint", {"position": v(236.7, -175.4) * mm});
            skLineSegment(sketch, "E228.4", {"start": v(224.98, -164.64) * mm, "end": v(233.8, -164.09) * mm});
            skLineSegment(sketch, "E228.3", {"start": v(221.04, -172.54) * mm, "end": v(224.98, -164.64) * mm});
            skLineSegment(sketch, "E228.1", {"start": v(234.74, -179.36) * mm, "end": v(225.92, -179.9) * mm});
            skLineSegment(sketch, "E228.0", {"start": v(238.68, -171.45) * mm, "end": v(234.74, -179.36) * mm});
            skLineSegment(sketch, "E228.2", {"start": v(225.92, -179.9) * mm, "end": v(221.04, -172.54) * mm});
            skLineSegment(sketch, "E228.5", {"start": v(233.8, -164.09) * mm, "end": v(238.68, -171.45) * mm});
            skPoint(sketch, "E229.0.midPoint", {"position": v(218.2, -185.1) * mm});
            skLineSegment(sketch, "E229.4", {"start": v(206.47, -174.33) * mm, "end": v(215.29, -173.78) * mm});
            skLineSegment(sketch, "E229.3", {"start": v(202.54, -182.24) * mm, "end": v(206.47, -174.33) * mm});
            skLineSegment(sketch, "E229.1", {"start": v(216.24, -189.05) * mm, "end": v(207.42, -189.6) * mm});
            skLineSegment(sketch, "E229.0", {"start": v(220.17, -181.14) * mm, "end": v(216.24, -189.05) * mm});
            skLineSegment(sketch, "E229.2", {"start": v(207.42, -189.6) * mm, "end": v(202.54, -182.24) * mm});
            skLineSegment(sketch, "E229.5", {"start": v(215.29, -173.78) * mm, "end": v(220.17, -181.14) * mm});
            skPoint(sketch, "E230.0.midPoint", {"position": v(253.7, -163.1) * mm});
            skLineSegment(sketch, "E230.4", {"start": v(241.98, -152.34) * mm, "end": v(250.8, -151.8) * mm});
            skLineSegment(sketch, "E230.3", {"start": v(238.04, -160.25) * mm, "end": v(241.98, -152.34) * mm});
            skLineSegment(sketch, "E230.1", {"start": v(251.74, -167.06) * mm, "end": v(242.92, -167.6) * mm});
            skLineSegment(sketch, "E230.0", {"start": v(255.68, -159.15) * mm, "end": v(251.74, -167.06) * mm});
            skLineSegment(sketch, "E230.2", {"start": v(242.92, -167.6) * mm, "end": v(238.04, -160.25) * mm});
            skLineSegment(sketch, "E230.5", {"start": v(250.8, -151.8) * mm, "end": v(255.68, -159.15) * mm});
            skPoint(sketch, "E231.0.midPoint", {"position": v(273.75, -175.88) * mm});
            skLineSegment(sketch, "E231.4", {"start": v(262.02, -165.11) * mm, "end": v(270.84, -164.56) * mm});
            skLineSegment(sketch, "E231.3", {"start": v(258.09, -173.02) * mm, "end": v(262.02, -165.11) * mm});
            skLineSegment(sketch, "E231.1", {"start": v(271.79, -179.84) * mm, "end": v(262.97, -180.38) * mm});
            skLineSegment(sketch, "E231.0", {"start": v(275.72, -171.93) * mm, "end": v(271.79, -179.84) * mm});
            skLineSegment(sketch, "E231.2", {"start": v(262.97, -180.38) * mm, "end": v(258.09, -173.02) * mm});
            skLineSegment(sketch, "E231.5", {"start": v(270.84, -164.56) * mm, "end": v(275.72, -171.93) * mm});
            skPoint(sketch, "E232.0.midPoint", {"position": v(290.22, -164.39) * mm});
            skLineSegment(sketch, "E232.4", {"start": v(278.5, -153.62) * mm, "end": v(287.3, -153.07) * mm});
            skLineSegment(sketch, "E232.3", {"start": v(274.56, -161.52) * mm, "end": v(278.5, -153.62) * mm});
            skLineSegment(sketch, "E232.1", {"start": v(288.26, -168.34) * mm, "end": v(279.44, -168.89) * mm});
            skLineSegment(sketch, "E232.0", {"start": v(292.2, -160.43) * mm, "end": v(288.26, -168.34) * mm});
            skLineSegment(sketch, "E232.2", {"start": v(279.44, -168.89) * mm, "end": v(274.56, -161.52) * mm});
            skLineSegment(sketch, "E232.5", {"start": v(287.3, -153.07) * mm, "end": v(292.2, -160.43) * mm});
            skLineSegment(sketch, "E233.MirrorCS", {"start": v(337.44, -153.62) * mm, "end": v(328.62, -153.07) * mm});
            skLineSegment(sketch, "E234.MirrorCS", {"start": v(341.37, -161.52) * mm, "end": v(337.44, -153.62) * mm});
            skLineSegment(sketch, "E235.MirrorCS", {"start": v(328.62, -153.07) * mm, "end": v(323.74, -160.43) * mm});
            skPoint(sketch, "E236.MirrorP", {"position": v(325.7, -164.39) * mm});
            skLineSegment(sketch, "E237.MirrorCS", {"start": v(323.74, -160.43) * mm, "end": v(327.67, -168.34) * mm});
            skLineSegment(sketch, "E238.MirrorCS", {"start": v(327.67, -168.34) * mm, "end": v(336.5, -168.89) * mm});
            skLineSegment(sketch, "E239.MirrorCS", {"start": v(336.5, -168.89) * mm, "end": v(341.37, -161.52) * mm});
            skLineSegment(sketch, "E240.MirrorCS", {"start": v(409.46, -174.33) * mm, "end": v(400.64, -173.78) * mm});
            skLineSegment(sketch, "E241.MirrorCS", {"start": v(402.73, -166.38) * mm, "end": v(411.55, -166.93) * mm});
            skLineSegment(sketch, "E242.MirrorCS", {"start": v(364.19, -167.06) * mm, "end": v(373, -167.6) * mm});
            skLineSegment(sketch, "E243.MirrorCS", {"start": v(390.95, -164.64) * mm, "end": v(382.13, -164.09) * mm});
            skLineSegment(sketch, "E244.MirrorCS", {"start": v(400.64, -173.78) * mm, "end": v(395.76, -181.14) * mm});
            skPoint(sketch, "E245.MirrorP", {"position": v(362.22, -163.1) * mm});
            skLineSegment(sketch, "E246.MirrorCS", {"start": v(360.25, -159.15) * mm, "end": v(364.19, -167.06) * mm});
            skLineSegment(sketch, "E247.MirrorCS", {"start": v(394.89, -172.54) * mm, "end": v(390.95, -164.64) * mm});
            skLineSegment(sketch, "E248.MirrorCS", {"start": v(344.14, -179.84) * mm, "end": v(352.96, -180.38) * mm});
            skPoint(sketch, "E249.MirrorP", {"position": v(400.76, -162.43) * mm});
            skLineSegment(sketch, "E250.MirrorCS", {"start": v(373, -167.6) * mm, "end": v(377.89, -160.25) * mm});
            skLineSegment(sketch, "E251.MirrorCS", {"start": v(395.76, -181.14) * mm, "end": v(399.7, -189.05) * mm});
            skLineSegment(sketch, "E252.MirrorCS", {"start": v(377.25, -171.45) * mm, "end": v(381.19, -179.36) * mm});
            skPoint(sketch, "E253.MirrorP", {"position": v(379.22, -175.4) * mm});
            skLineSegment(sketch, "E254.MirrorCS", {"start": v(381.19, -179.36) * mm, "end": v(390, -179.9) * mm});
            skLineSegment(sketch, "E255.MirrorCS", {"start": v(382.13, -164.09) * mm, "end": v(377.25, -171.45) * mm});
            skLineSegment(sketch, "E256.MirrorCS", {"start": v(357.84, -173.02) * mm, "end": v(353.9, -165.11) * mm});
            skLineSegment(sketch, "E257.MirrorCS", {"start": v(352.96, -180.38) * mm, "end": v(357.84, -173.02) * mm});
            skLineSegment(sketch, "E258.MirrorCS", {"start": v(377.89, -160.25) * mm, "end": v(373.95, -152.34) * mm});
            skPoint(sketch, "E259.MirrorP", {"position": v(342.18, -175.88) * mm});
            skLineSegment(sketch, "E260.MirrorCS", {"start": v(390, -179.9) * mm, "end": v(394.89, -172.54) * mm});
            skLineSegment(sketch, "E261.MirrorCS", {"start": v(373.95, -152.34) * mm, "end": v(365.14, -151.8) * mm});
            skLineSegment(sketch, "E262.MirrorCS", {"start": v(340.2, -171.93) * mm, "end": v(344.14, -179.84) * mm});
            skLineSegment(sketch, "E263.MirrorCS", {"start": v(353.9, -165.11) * mm, "end": v(345.09, -164.56) * mm});
            skLineSegment(sketch, "E264.MirrorCS", {"start": v(365.14, -151.8) * mm, "end": v(360.25, -159.15) * mm});
            skLineSegment(sketch, "E265.MirrorCS", {"start": v(345.09, -164.56) * mm, "end": v(340.2, -171.93) * mm});
            skLineSegment(sketch, "E266.MirrorCS", {"start": v(399.7, -189.05) * mm, "end": v(408.51, -189.6) * mm});
            skLineSegment(sketch, "E267.MirrorCS", {"start": v(408.51, -189.6) * mm, "end": v(413.4, -182.24) * mm});
            skLineSegment(sketch, "E268.MirrorCS", {"start": v(413.4, -182.24) * mm, "end": v(409.46, -174.33) * mm});
            skLineSegment(sketch, "E269.MirrorCS", {"start": v(411.55, -166.93) * mm, "end": v(416.43, -159.57) * mm});
            skLineSegment(sketch, "E270.MirrorCS", {"start": v(416.43, -159.57) * mm, "end": v(412.5, -151.66) * mm});
            skLineSegment(sketch, "E271.MirrorCS", {"start": v(412.5, -151.66) * mm, "end": v(403.68, -151.11) * mm});
            skLineSegment(sketch, "E272.MirrorCS", {"start": v(403.68, -151.11) * mm, "end": v(398.8, -158.47) * mm});
            skLineSegment(sketch, "E273.MirrorCS", {"start": v(398.8, -158.47) * mm, "end": v(402.73, -166.38) * mm});
            skArc(sketch, "E274", {"start": v(294.45, -137.78) * mm, "mid": v(307.96, -151.73) * mm, "end": v(321.48, -137.78) * mm});
            skPoint(sketch, "E275", {"position": v(443, -157.78) * mm});
            skPoint(sketch, "E276", {"position": v(443, -161.78) * mm});
            skLineSegment(sketch, "E277", {"start": v(443, -157.78) * mm, "end": v(435, -157.78) * mm});
            skLineSegment(sketch, "E278", {"start": v(435, -157.78) * mm, "end": v(435, -161.78) * mm});
            skLineSegment(sketch, "E279", {"start": v(435, -161.78) * mm, "end": v(443, -161.78) * mm});
            skLineSegment(sketch, "E280.MirrorCS", {"start": v(180.93, -161.78) * mm, "end": v(172.93, -161.78) * mm});
            skLineSegment(sketch, "E281.MirrorCS", {"start": v(172.93, -157.78) * mm, "end": v(180.93, -157.78) * mm});
            skLineSegment(sketch, "E282.MirrorCS", {"start": v(180.93, -157.78) * mm, "end": v(180.93, -161.78) * mm});
            skPoint(sketch, "E283.orphan", {"position": v(286.93, -201.78) * mm});
            skPoint(sketch, "E284.orphan", {"position": v(329, -201.78) * mm});
            skLineSegment(sketch, "E285.trimOffspring", {"start": v(443, -161.78) * mm, "end": v(443, -201.78) * mm});
            skLineSegment(sketch, "E286.trimOffspring", {"start": v(172.93, -161.78) * mm, "end": v(172.93, -201.78) * mm});
            skLineSegment(sketch, "E287.MirrorCS", {"start": v(227.16, -211) * mm, "end": v(227.16, -226.44) * mm});
            skLineSegment(sketch, "E288.MirrorCS", {"start": v(222.96, -226.44) * mm, "end": v(222.96, -211) * mm});
            skLineSegment(sketch, "E289.MirrorCS", {"start": v(227.16, -211) * mm, "end": v(223.16, -211) * mm});
            skLineSegment(sketch, "E290.MirrorCS", {"start": v(227.16, -226.44) * mm, "end": v(223.16, -226.44) * mm});
            skLineSegment(sketch, "E291", {"start": v(392.68, -226.44) * mm, "end": v(392.68, -211) * mm});
            skLineSegment(sketch, "E292", {"start": v(388.68, -226.44) * mm, "end": v(392.68, -226.44) * mm});
            skLineSegment(sketch, "E293.trimOffspring", {"start": v(388.68, -211) * mm, "end": v(388.68, -226.44) * mm});
            skLineSegment(sketch, "E294", {"start": v(388.68, -211) * mm, "end": v(392.68, -211) * mm});
            skLineSegment(sketch, "E295", {"start": v(388.68, -218.72) * mm, "end": v(227.16, -218.72) * mm, "construction": true});
            skPoint(sketch, "E296", {"position": v(307.92, -218.72) * mm});
            skLineSegment(sketch, "E297", {"start": v(307.96, -138.21) * mm, "end": v(307.96, -268.31) * mm, "construction": true});
            skLineSegment(sketch, "E298", {"start": v(222.96, -211) * mm, "end": v(222.96, -126.94) * mm, "construction": true});
            skPoint(sketch, "E299", {"position": v(222.96, -181.95) * mm});
            skPoint(sketch, "E300", {"position": v(222.96, -201.78) * mm});
            skPoint(sketch, "E301", {"position": v(222.96, -161.95) * mm});
            skLineSegment(sketch, "E302", {"start": v(392.68, -211) * mm, "end": v(392.68, -131.14) * mm, "construction": true});
            skLineSegment(sketch, "E303", {"start": v(227.16, -211) * mm, "end": v(227.16, -120.97) * mm, "construction": true});
            skLineSegment(sketch, "E304", {"start": v(388.68, -211) * mm, "end": v(388.68, -120.97) * mm, "construction": true});
            skLineSegment(sketch, "E305", {"start": v(222.96, -161.95) * mm, "end": v(503.9, -161.95) * mm, "construction": true});
            skLineSegment(sketch, "E306", {"start": v(222.96, -181.95) * mm, "end": v(493.21, -181.95) * mm, "construction": true});
            skLineSegment(sketch, "E307.bottom", {"start": v(222.96, -161.95) * mm, "end": v(227.16, -161.95) * mm});
            skLineSegment(sketch, "E307.top", {"start": v(222.96, -181.95) * mm, "end": v(227.16, -181.95) * mm});
            skLineSegment(sketch, "E307.left", {"start": v(222.96, -161.95) * mm, "end": v(222.96, -181.95) * mm});
            skLineSegment(sketch, "E307.right", {"start": v(227.16, -161.95) * mm, "end": v(227.16, -181.95) * mm});
            skLineSegment(sketch, "E308.bottom", {"start": v(388.68, -161.95) * mm, "end": v(392.68, -161.95) * mm});
            skLineSegment(sketch, "E308.top", {"start": v(388.68, -181.95) * mm, "end": v(392.68, -181.95) * mm});
            skLineSegment(sketch, "E308.left", {"start": v(388.68, -161.95) * mm, "end": v(388.68, -181.95) * mm});
            skLineSegment(sketch, "E308.right", {"start": v(392.68, -161.95) * mm, "end": v(392.68, -181.95) * mm});
            skLineSegment(sketch, "E309", {"start": v(402.73, -166.38) * mm, "end": v(402.73, -173.9) * mm, "construction": true});
            skLineSegment(sketch, "E310", {"start": v(213.2, -166.38) * mm, "end": v(213.66, -173.88) * mm, "construction": true});
            skCircle(sketch, "E311", {"center": v(213.43, -170.13) * mm, "radius": 2 * mm});
            skCircle(sketch, "E312", {"center": v(402.73, -170.15) * mm, "radius": 2 * mm});
            skLineSegment(sketch, "E313", {"start": v(213.43, -170.13) * mm, "end": v(222.96, -170.13) * mm, "construction": true});
            skSolve(sketch);
        }
        {
            var Q0;
            Q0=makeQuery(id+"F8.imprint","IMPRINT",FACE,{"disambiguationData":[TD([[makeQuery(id+"F8.imprint","IMPRINT",EDGE,{"derivedFrom":sQuery(id+"F8.wireOp",EDGE,"E214")}),-1.0]])]});
            var Q1;
            Q1=makeQuery(id+"F8.imprint","IMPRINT",FACE,{"disambiguationData":[TD([[makeQuery(id+"F8.imprint","IMPRINT",EDGE,{"derivedFrom":sQuery(id+"F8.wireOp",EDGE,"E219.MirrorC")}),1.0]])]});
            var Q2;
            {var subQ0=sQuery(id+"F8.wireOp",EDGE,"E228.2");var subQ1=sQuery(id+"F8.wireOp",EDGE,"E228.3");var subQ2=makeQuery(id+"F8.imprint","INTERSECT",VERTEX,{"derivedFrom":[subQ1,subQ0]});Q2=makeQuery(id+"F8.imprint","IMPRINT",FACE,{"disambiguationData":[TD([[makeQuery(id+"F8.imprint","IMPRINT",EDGE,{"disambiguationData":[TD([[subQ2,-1.0]])],"derivedFrom":subQ1}),-1.0]])]});}
            var Q3;
            {var subQ0=sQuery(id+"F8.wireOp",EDGE,"E260.MirrorCS");var subQ1=sQuery(id+"F8.wireOp",EDGE,"E247.MirrorCS");var subQ2=makeQuery(id+"F8.imprint","INTERSECT",VERTEX,{"derivedFrom":[subQ1,subQ0]});Q3=makeQuery(id+"F8.imprint","IMPRINT",FACE,{"disambiguationData":[TD([[makeQuery(id+"F8.imprint","IMPRINT",EDGE,{"disambiguationData":[TD([[subQ2,-1.0]])],"derivedFrom":subQ1}),1.0]])]});}
            extrude(context, id + "F9", {"entities" : qUnion([Q0, Q1, Q2, Q3]), "depth" : 4 * mm});
        }
        {
            var Q0;
            Q0=makeQuery(id+"F8.imprint","IMPRINT",FACE,{"disambiguationData":[TD([[makeQuery(id+"F8.imprint","IMPRINT",EDGE,{"derivedFrom":sQuery(id+"F8.wireOp",EDGE,"E233.MirrorCS")}),1.0]])]});
            var Q1;
            Q1=makeQuery(id+"F8.imprint","IMPRINT",FACE,{"disambiguationData":[TD([[makeQuery(id+"F8.imprint","IMPRINT",EDGE,{"derivedFrom":sQuery(id+"F8.wireOp",EDGE,"E232.4")}),-1.0]])]});
            var Q2;
            Q2=makeQuery(id+"F8.imprint","IMPRINT",FACE,{"disambiguationData":[TD([[makeQuery(id+"F8.imprint","IMPRINT",EDGE,{"derivedFrom":sQuery(id+"F8.wireOp",EDGE,"E231.4")}),-1.0]])]});
            var Q3;
            Q3=makeQuery(id+"F8.imprint","IMPRINT",FACE,{"disambiguationData":[TD([[makeQuery(id+"F8.imprint","IMPRINT",EDGE,{"derivedFrom":sQuery(id+"F8.wireOp",EDGE,"E230.4")}),-1.0]])]});
            var Q4;
            Q4=makeQuery(id+"F8.imprint","IMPRINT",FACE,{"disambiguationData":[TD([[makeQuery(id+"F8.imprint","IMPRINT",EDGE,{"derivedFrom":sQuery(id+"F8.wireOp",EDGE,"E228.4")}),-1.0]])]});
            var Q5;
            Q5=makeQuery(id+"F8.imprint","IMPRINT",FACE,{"disambiguationData":[TD([[makeQuery(id+"F8.imprint","IMPRINT",EDGE,{"derivedFrom":sQuery(id+"F8.wireOp",EDGE,"E227.0")}),-1.0]])]});
            var Q6;
            Q6=makeQuery(id+"F8.imprint","IMPRINT",FACE,{"disambiguationData":[TD([[makeQuery(id+"F8.imprint","IMPRINT",EDGE,{"derivedFrom":sQuery(id+"F8.wireOp",EDGE,"E248.MirrorCS")}),1.0]])]});
            var Q7;
            Q7=makeQuery(id+"F8.imprint","IMPRINT",FACE,{"disambiguationData":[TD([[makeQuery(id+"F8.imprint","IMPRINT",EDGE,{"derivedFrom":sQuery(id+"F8.wireOp",EDGE,"E242.MirrorCS")}),1.0]])]});
            var Q8;
            Q8=makeQuery(id+"F8.imprint","IMPRINT",FACE,{"disambiguationData":[TD([[makeQuery(id+"F8.imprint","IMPRINT",EDGE,{"derivedFrom":sQuery(id+"F8.wireOp",EDGE,"E243.MirrorCS")}),1.0]])]});
            var Q9;
            Q9=makeQuery(id+"F8.imprint","IMPRINT",FACE,{"disambiguationData":[TD([[makeQuery(id+"F8.imprint","IMPRINT",EDGE,{"derivedFrom":sQuery(id+"F8.wireOp",EDGE,"E241.MirrorCS")}),1.0]])]});
            var Q10;
            Q10=makeQuery(id+"F8.imprint","IMPRINT",FACE,{"disambiguationData":[TD([[makeQuery(id+"F8.imprint","IMPRINT",EDGE,{"derivedFrom":sQuery(id+"F8.wireOp",EDGE,"E229.4")}),-1.0]])]});
            var Q11;
            Q11=makeQuery(id+"F8.imprint","IMPRINT",FACE,{"disambiguationData":[TD([[makeQuery(id+"F8.imprint","IMPRINT",EDGE,{"derivedFrom":sQuery(id+"F8.wireOp",EDGE,"E240.MirrorCS")}),1.0]])]});
            extrude(context, id + "F10", {"entities" : qUnion([Q0, Q1, Q2, Q3, Q4, Q5, Q6, Q7, Q8, Q9, Q10, Q11]), "operationType" : NewBodyOperationType.ADD, "depth" : 3.5 * mm});
        }
        {
            var Q0;
            Q0=qCreatedBy(makeId("Top.planeOp"),FACE);
            var sketch = newSketch(context, id + "F11", { "sketchPlane" : qUnion([Q0])});
            skCircle(sketch, "E314", {"center": v(119.17, 58.1) * mm, "radius": 2 * mm});
            skArc(sketch, "E315", {"start": v(255.65, 48.1) * mm, "mid": v(244.2, 48.35) * mm, "end": v(232.76, 48.1) * mm});
            skLineSegment(sketch, "E316.MirrorCS", {"start": v(109.17, 92.1) * mm, "end": v(109.17, 82.1) * mm});
            skCircle(sketch, "E317.MirrorC", {"center": v(119.17, 82.1) * mm, "radius": 2 * mm});
            skLineSegment(sketch, "E318", {"start": v(379.24, 92.1) * mm, "end": v(379.24, 82.3) * mm});
            skPoint(sketch, "E319.0.midPoint", {"position": v(172.95, 64.48) * mm});
            skLineSegment(sketch, "E319.4", {"start": v(161.22, 75.25) * mm, "end": v(170.03, 75.8) * mm});
            skLineSegment(sketch, "E319.3", {"start": v(157.28, 67.34) * mm, "end": v(161.22, 75.25) * mm});
            skLineSegment(sketch, "E319.1", {"start": v(170.98, 60.53) * mm, "end": v(162.16, 59.98) * mm});
            skLineSegment(sketch, "E319.0", {"start": v(174.91, 68.43) * mm, "end": v(170.98, 60.53) * mm});
            skCircle(sketch, "E319.cCircle", {"center": v(166.1, 67.89) * mm, "radius": 7.65 * mm, "construction": true});
            skLineSegment(sketch, "E319.2", {"start": v(162.16, 59.98) * mm, "end": v(157.28, 67.34) * mm});
            skLineSegment(sketch, "E319.5", {"start": v(170.03, 75.8) * mm, "end": v(174.91, 68.43) * mm});
            skPoint(sketch, "E320.0.midPoint", {"position": v(154.44, 54.79) * mm});
            skLineSegment(sketch, "E320.4", {"start": v(142.7, 65.56) * mm, "end": v(151.53, 66.1) * mm});
            skLineSegment(sketch, "E320.3", {"start": v(138.77, 57.65) * mm, "end": v(142.7, 65.56) * mm});
            skLineSegment(sketch, "E320.1", {"start": v(152.47, 50.84) * mm, "end": v(143.66, 50.29) * mm});
            skLineSegment(sketch, "E320.0", {"start": v(156.4, 58.74) * mm, "end": v(152.47, 50.84) * mm});
            skCircle(sketch, "E320.cCircle", {"center": v(147.6, 58.2) * mm, "radius": 7.65 * mm, "construction": true});
            skLineSegment(sketch, "E320.2", {"start": v(143.66, 50.29) * mm, "end": v(138.77, 57.65) * mm});
            skLineSegment(sketch, "E320.5", {"start": v(151.53, 66.1) * mm, "end": v(156.4, 58.74) * mm});
            skPoint(sketch, "E321.0.midPoint", {"position": v(189.95, 76.78) * mm});
            skLineSegment(sketch, "E321.4", {"start": v(178.21, 87.55) * mm, "end": v(187.03, 88.1) * mm});
            skLineSegment(sketch, "E321.3", {"start": v(174.28, 79.64) * mm, "end": v(178.21, 87.55) * mm});
            skLineSegment(sketch, "E321.1", {"start": v(187.98, 72.82) * mm, "end": v(179.16, 72.28) * mm});
            skLineSegment(sketch, "E321.0", {"start": v(191.91, 80.73) * mm, "end": v(187.98, 72.82) * mm});
            skCircle(sketch, "E321.cCircle", {"center": v(183.1, 80.19) * mm, "radius": 7.65 * mm, "construction": true});
            skLineSegment(sketch, "E321.2", {"start": v(179.16, 72.28) * mm, "end": v(174.28, 79.64) * mm});
            skLineSegment(sketch, "E321.5", {"start": v(187.03, 88.1) * mm, "end": v(191.91, 80.73) * mm});
            skPoint(sketch, "E322.0.midPoint", {"position": v(210, 64) * mm});
            skLineSegment(sketch, "E322.4", {"start": v(198.26, 74.78) * mm, "end": v(207.08, 75.32) * mm});
            skLineSegment(sketch, "E322.3", {"start": v(194.33, 66.87) * mm, "end": v(198.26, 74.78) * mm});
            skLineSegment(sketch, "E322.1", {"start": v(208.02, 60.05) * mm, "end": v(199.2, 59.5) * mm});
            skLineSegment(sketch, "E322.0", {"start": v(211.96, 67.96) * mm, "end": v(208.02, 60.05) * mm});
            skCircle(sketch, "E322.cCircle", {"center": v(203.14, 67.41) * mm, "radius": 7.65 * mm, "construction": true});
            skLineSegment(sketch, "E322.2", {"start": v(199.2, 59.5) * mm, "end": v(194.33, 66.87) * mm});
            skLineSegment(sketch, "E322.5", {"start": v(207.08, 75.32) * mm, "end": v(211.96, 67.96) * mm});
            skPoint(sketch, "E323.0.midPoint", {"position": v(226.46, 75.5) * mm});
            skLineSegment(sketch, "E323.4", {"start": v(214.73, 86.27) * mm, "end": v(223.55, 86.82) * mm});
            skLineSegment(sketch, "E323.3", {"start": v(210.8, 78.36) * mm, "end": v(214.73, 86.27) * mm});
            skLineSegment(sketch, "E323.1", {"start": v(224.5, 71.55) * mm, "end": v(215.68, 71) * mm});
            skLineSegment(sketch, "E323.0", {"start": v(228.43, 79.45) * mm, "end": v(224.5, 71.55) * mm});
            skCircle(sketch, "E323.cCircle", {"center": v(219.61, 78.9) * mm, "radius": 7.65 * mm, "construction": true});
            skLineSegment(sketch, "E323.2", {"start": v(215.68, 71) * mm, "end": v(210.8, 78.36) * mm});
            skLineSegment(sketch, "E323.5", {"start": v(223.55, 86.82) * mm, "end": v(228.43, 79.45) * mm});
            skLineSegment(sketch, "E324.MirrorCS", {"start": v(273.68, 86.27) * mm, "end": v(264.86, 86.82) * mm});
            skLineSegment(sketch, "E325.MirrorCS", {"start": v(277.61, 78.36) * mm, "end": v(273.68, 86.27) * mm});
            skLineSegment(sketch, "E326.MirrorCS", {"start": v(264.86, 86.82) * mm, "end": v(259.98, 79.45) * mm});
            skPoint(sketch, "E327.MirrorP", {"position": v(261.94, 75.5) * mm});
            skLineSegment(sketch, "E328.MirrorCS", {"start": v(259.98, 79.45) * mm, "end": v(263.91, 71.55) * mm});
            skLineSegment(sketch, "E329.MirrorCS", {"start": v(263.91, 71.55) * mm, "end": v(272.73, 71) * mm});
            skLineSegment(sketch, "E330.MirrorCS", {"start": v(272.73, 71) * mm, "end": v(277.61, 78.36) * mm});
            skLineSegment(sketch, "E331.MirrorCS", {"start": v(345.7, 65.56) * mm, "end": v(336.88, 66.1) * mm});
            skLineSegment(sketch, "E332.MirrorCS", {"start": v(300.43, 72.82) * mm, "end": v(309.24, 72.28) * mm});
            skLineSegment(sketch, "E333.MirrorCS", {"start": v(327.2, 75.25) * mm, "end": v(318.37, 75.8) * mm});
            skLineSegment(sketch, "E334.MirrorCS", {"start": v(336.88, 66.1) * mm, "end": v(332, 58.74) * mm});
            skPoint(sketch, "E335.MirrorP", {"position": v(298.46, 76.78) * mm});
            skLineSegment(sketch, "E336.MirrorCS", {"start": v(296.5, 80.73) * mm, "end": v(300.43, 72.82) * mm});
            skLineSegment(sketch, "E337.MirrorCS", {"start": v(331.13, 67.34) * mm, "end": v(327.2, 75.25) * mm});
            skLineSegment(sketch, "E338.MirrorCS", {"start": v(280.38, 60.05) * mm, "end": v(289.2, 59.5) * mm});
            skLineSegment(sketch, "E339.MirrorCS", {"start": v(309.24, 72.28) * mm, "end": v(314.13, 79.64) * mm});
            skLineSegment(sketch, "E340.MirrorCS", {"start": v(332, 58.74) * mm, "end": v(335.93, 50.84) * mm});
            skLineSegment(sketch, "E341.MirrorCS", {"start": v(313.5, 68.43) * mm, "end": v(317.43, 60.53) * mm});
            skPoint(sketch, "E342.MirrorP", {"position": v(315.46, 64.48) * mm});
            skLineSegment(sketch, "E343.MirrorCS", {"start": v(317.43, 60.53) * mm, "end": v(326.24, 59.98) * mm});
            skLineSegment(sketch, "E344.MirrorCS", {"start": v(318.37, 75.8) * mm, "end": v(313.5, 68.43) * mm});
            skLineSegment(sketch, "E345.MirrorCS", {"start": v(294.08, 66.87) * mm, "end": v(290.14, 74.78) * mm});
            skLineSegment(sketch, "E346.MirrorCS", {"start": v(289.2, 59.5) * mm, "end": v(294.08, 66.87) * mm});
            skLineSegment(sketch, "E347.MirrorCS", {"start": v(314.13, 79.64) * mm, "end": v(310.2, 87.55) * mm});
            skPoint(sketch, "E348.MirrorP", {"position": v(278.41, 64) * mm});
            skLineSegment(sketch, "E349.MirrorCS", {"start": v(326.24, 59.98) * mm, "end": v(331.13, 67.34) * mm});
            skLineSegment(sketch, "E350.MirrorCS", {"start": v(310.2, 87.55) * mm, "end": v(301.37, 88.1) * mm});
            skLineSegment(sketch, "E351.MirrorCS", {"start": v(276.45, 67.96) * mm, "end": v(280.38, 60.05) * mm});
            skLineSegment(sketch, "E352.MirrorCS", {"start": v(290.14, 74.78) * mm, "end": v(281.33, 75.32) * mm});
            skLineSegment(sketch, "E353.MirrorCS", {"start": v(301.37, 88.1) * mm, "end": v(296.5, 80.73) * mm});
            skLineSegment(sketch, "E354.MirrorCS", {"start": v(281.33, 75.32) * mm, "end": v(276.45, 67.96) * mm});
            skLineSegment(sketch, "E355.MirrorCS", {"start": v(335.93, 50.84) * mm, "end": v(344.75, 50.29) * mm});
            skLineSegment(sketch, "E356.MirrorCS", {"start": v(344.75, 50.29) * mm, "end": v(349.63, 57.65) * mm});
            skLineSegment(sketch, "E357.MirrorCS", {"start": v(349.63, 57.65) * mm, "end": v(345.7, 65.56) * mm});
            skLineSegment(sketch, "E358.trimOffspring", {"start": v(379.24, 78.3) * mm, "end": v(379.24, 48.1) * mm});
            skLineSegment(sketch, "E359.trimOffspring", {"start": v(109.17, 78.1) * mm, "end": v(109.17, 48.1) * mm});
            skLineSegment(sketch, "E360", {"start": v(109.17, 78.1) * mm, "end": v(109.17, 82.1) * mm});
            skLineSegment(sketch, "E361", {"start": v(379.24, 78.3) * mm, "end": v(379.24, 82.3) * mm});
            skLineSegment(sketch, "E362", {"start": v(109.17, 92.1) * mm, "end": v(379.24, 92.1) * mm});
            skLineSegment(sketch, "E363", {"start": v(109.17, 48.1) * mm, "end": v(232.76, 48.1) * mm});
            skLineSegment(sketch, "E364.trimOffspring", {"start": v(255.65, 48.1) * mm, "end": v(379.24, 48.1) * mm});
            skCircle(sketch, "E365.MirrorC", {"center": v(369.24, 58.1) * mm, "radius": 2 * mm});
            skCircle(sketch, "E366.MirrorC", {"center": v(369.24, 82.1) * mm, "radius": 2 * mm});
            skSolve(sketch);
        }
        {
            var Q0;
            Q0=makeQuery(id+"F11.imprint","IMPRINT",FACE,{"disambiguationData":[TD([[makeQuery(id+"F11.imprint","IMPRINT",EDGE,{"derivedFrom":sQuery(id+"F11.wireOp",EDGE,"E314")}),-1.0]])]});
            extrude(context, id + "F12", {"entities" : qUnion([Q0]), "depth" : 4 * mm});
        }
        {
            var Q0;
            Q0=makeQuery(id+"F11.imprint","IMPRINT",FACE,{"disambiguationData":[TD([[makeQuery(id+"F11.imprint","IMPRINT",EDGE,{"derivedFrom":sQuery(id+"F11.wireOp",EDGE,"E320.4")}),-1.0]])]});
            var Q1;
            Q1=makeQuery(id+"F11.imprint","IMPRINT",FACE,{"disambiguationData":[TD([[makeQuery(id+"F11.imprint","IMPRINT",EDGE,{"derivedFrom":sQuery(id+"F11.wireOp",EDGE,"E319.4")}),-1.0]])]});
            var Q2;
            Q2=makeQuery(id+"F11.imprint","IMPRINT",FACE,{"disambiguationData":[TD([[makeQuery(id+"F11.imprint","IMPRINT",EDGE,{"derivedFrom":sQuery(id+"F11.wireOp",EDGE,"E321.4")}),-1.0]])]});
            var Q3;
            Q3=makeQuery(id+"F11.imprint","IMPRINT",FACE,{"disambiguationData":[TD([[makeQuery(id+"F11.imprint","IMPRINT",EDGE,{"derivedFrom":sQuery(id+"F11.wireOp",EDGE,"E322.4")}),-1.0]])]});
            var Q4;
            Q4=makeQuery(id+"F11.imprint","IMPRINT",FACE,{"disambiguationData":[TD([[makeQuery(id+"F11.imprint","IMPRINT",EDGE,{"derivedFrom":sQuery(id+"F11.wireOp",EDGE,"E323.4")}),-1.0]])]});
            var Q5;
            Q5=makeQuery(id+"F11.imprint","IMPRINT",FACE,{"disambiguationData":[TD([[makeQuery(id+"F11.imprint","IMPRINT",EDGE,{"derivedFrom":sQuery(id+"F11.wireOp",EDGE,"E324.MirrorCS")}),1.0]])]});
            var Q6;
            Q6=makeQuery(id+"F11.imprint","IMPRINT",FACE,{"disambiguationData":[TD([[makeQuery(id+"F11.imprint","IMPRINT",EDGE,{"derivedFrom":sQuery(id+"F11.wireOp",EDGE,"E338.MirrorCS")}),1.0]])]});
            var Q7;
            Q7=makeQuery(id+"F11.imprint","IMPRINT",FACE,{"disambiguationData":[TD([[makeQuery(id+"F11.imprint","IMPRINT",EDGE,{"derivedFrom":sQuery(id+"F11.wireOp",EDGE,"E332.MirrorCS")}),1.0]])]});
            var Q8;
            Q8=makeQuery(id+"F11.imprint","IMPRINT",FACE,{"disambiguationData":[TD([[makeQuery(id+"F11.imprint","IMPRINT",EDGE,{"derivedFrom":sQuery(id+"F11.wireOp",EDGE,"E333.MirrorCS")}),1.0]])]});
            var Q9;
            Q9=makeQuery(id+"F11.imprint","IMPRINT",FACE,{"disambiguationData":[TD([[makeQuery(id+"F11.imprint","IMPRINT",EDGE,{"derivedFrom":sQuery(id+"F11.wireOp",EDGE,"E331.MirrorCS")}),1.0]])]});
            extrude(context, id + "F13", {"entities" : qUnion([Q0, Q1, Q2, Q3, Q4, Q5, Q6, Q7, Q8, Q9]), "operationType" : NewBodyOperationType.ADD, "depth" : 3.5 * mm});
        }
        {
            var Q0;
            Q0=qCreatedBy(makeId("Top.planeOp"),FACE);
            var sketch = newSketch(context, id + "F14", { "sketchPlane" : qUnion([Q0])});
            skCircle(sketch, "E367", {"center": v(796.44, 289.28) * mm, "radius": 2 * mm});
            skCircle(sketch, "E368", {"center": v(819.44, 289.28) * mm, "radius": 2 * mm});
            skCircle(sketch, "E369", {"center": v(807.94, 289.28) * mm, "radius": 4 * mm});
            skLineSegment(sketch, "E370", {"start": v(969.62, -46.4) * mm, "end": v(969.62, 307.18) * mm});
            skLineSegment(sketch, "E371.MirrorCS", {"start": v(646.85, -46.4) * mm, "end": v(646.85, 307.18) * mm});
            skCircle(sketch, "E372", {"center": v(656.85, 130) * mm, "radius": 2 * mm});
            skPoint(sketch, "E373", {"position": v(656.85, 290) * mm});
            skCircle(sketch, "E374", {"center": v(656.85, 290) * mm, "radius": 2 * mm});
            skPoint(sketch, "E375", {"position": v(656.85, -30) * mm});
            skCircle(sketch, "E376", {"center": v(656.85, -30) * mm, "radius": 2 * mm});
            skCircle(sketch, "E377.MirrorC", {"center": v(959.62, 130) * mm, "radius": 2 * mm});
            skCircle(sketch, "E378.MirrorC", {"center": v(959.62, -30) * mm, "radius": 2 * mm});
            skCircle(sketch, "E379.MirrorC", {"center": v(959.62, 290) * mm, "radius": 2 * mm});
            skLineSegment(sketch, "E380", {"start": v(646.85, 307.18) * mm, "end": v(790.75, 307.18) * mm});
            skLineSegment(sketch, "E381", {"start": v(646.85, -46.4) * mm, "end": v(969.62, -46.4) * mm});
            skLineSegment(sketch, "E382.trimOffspring", {"start": v(825.24, 307.18) * mm, "end": v(969.62, 307.18) * mm});
            skLineSegment(sketch, "E383", {"start": v(790.75, 307.18) * mm, "end": v(825.24, 307.18) * mm});
            skLineSegment(sketch, "E384", {"start": v(646.85, 130.4) * mm, "end": v(922.02, 130.4) * mm, "construction": true});
            skCircle(sketch, "E385.MirrorC", {"center": v(796.44, -28.5) * mm, "radius": 2 * mm});
            skCircle(sketch, "E386.MirrorC", {"center": v(807.94, -28.5) * mm, "radius": 4 * mm});
            skCircle(sketch, "E387.MirrorC", {"center": v(819.44, -28.5) * mm, "radius": 2 * mm});
            skSolve(sketch);
        }
        {
            var Q0;
            Q0=makeQuery(id+"F14.imprint","IMPRINT",FACE,{"disambiguationData":[TD([[makeQuery(id+"F14.imprint","IMPRINT",EDGE,{"derivedFrom":sQuery(id+"F14.wireOp",EDGE,"23d373e1-426d-40cf-81d0-1c8116d77816.right")}),1.0]])]});
            var Q1;
            {var subQ10=sQuery(id+"F14.wireOp",EDGE,"3c6c79d6-9cef-4f63-96dc-ad248f381b62.bottom");Q1=makeQuery(id+"F14.imprint","IMPRINT",FACE,{"disambiguationData":[TD([[makeQuery(id+"F14.imprint","IMPRINT",EDGE,{"derivedFrom":subQ10}),-1.0]])]});}
            var Q2;
            {var subQ8=sQuery(id+"F14.wireOp",EDGE,"6cf56efc-ad20-4e1a-a414-00fd335aa3e3");Q2=makeQuery(id+"F14.imprint","IMPRINT",FACE,{"disambiguationData":[TD([[makeQuery(id+"F14.imprint","IMPRINT",EDGE,{"derivedFrom":subQ8}),1.0]])]});}
            var Q3;
            {var subQ1=sQuery(id+"F14.wireOp",EDGE,"E371.MirrorCS");Q3=makeQuery(id+"F14.imprint","IMPRINT",FACE,{"disambiguationData":[TD([[makeQuery(id+"F14.imprint","IMPRINT",EDGE,{"derivedFrom":subQ1}),-1.0]])]});}
            var Q4;
            {var subQ1=sQuery(id+"F14.wireOp",EDGE,"E370");Q4=makeQuery(id+"F14.imprint","IMPRINT",FACE,{"disambiguationData":[TD([[makeQuery(id+"F14.imprint","IMPRINT",EDGE,{"derivedFrom":subQ1}),1.0]])]});}
            var Q5;
            Q5=makeQuery(id+"F14.imprint","IMPRINT",FACE,{"disambiguationData":[TD([[makeQuery(id+"F14.imprint","IMPRINT",EDGE,{"derivedFrom":sQuery(id+"F14.wireOp",EDGE,"E367")}),-1.0]])]});
            extrude(context, id + "F15", {"entities" : qUnion([Q0, Q1, Q2, Q3, Q4, Q5]), "depth" : 4 * mm});
        }
        {
            var Q0;
            Q0=qCreatedBy(makeId("Top.planeOp"),FACE);
            var sketch = newSketch(context, id + "F16", { "sketchPlane" : qUnion([Q0])});
            skPoint(sketch, "E388", {"position": v(142.81, 363.62) * mm});
            skArc(sketch, "E389", {"start": v(142.81, 363.62) * mm, "mid": v(156.1, 336.9) * mm, "end": v(182.81, 323.62) * mm});
            skCircle(sketch, "E390", {"center": v(171.81, 313.62) * mm, "radius": 2 * mm});
            skCircle(sketch, "E391", {"center": v(151.81, 313.62) * mm, "radius": 2 * mm});
            skCircle(sketch, "E392", {"center": v(132.81, 352.62) * mm, "radius": 2 * mm});
            skCircle(sketch, "E393", {"center": v(132.81, 332.62) * mm, "radius": 2 * mm});
            skArc(sketch, "E394.filletArc", {"start": v(122.81, 308.62) * mm, "mid": v(124.28, 305.09) * mm, "end": v(127.81, 303.62) * mm});
            skCircle(sketch, "E395", {"center": v(132.81, 313.62) * mm, "radius": 2.5 * mm});
            skLineSegment(sketch, "E396", {"start": v(122.81, 303.62) * mm, "end": v(122.81, 638.62) * mm});
            skLineSegment(sketch, "E397", {"start": v(502.81, 638.62) * mm, "end": v(502.81, 308.62) * mm});
            skLineSegment(sketch, "E398", {"start": v(497.81, 303.62) * mm, "end": v(127.81, 303.62) * mm});
            skArc(sketch, "E399.MirrorCS", {"start": v(482.81, 363.62) * mm, "mid": v(469.53, 336.9) * mm, "end": v(442.81, 323.62) * mm});
            skArc(sketch, "E400.MirrorCS", {"start": v(142.81, 583.62) * mm, "mid": v(156.1, 610.34) * mm, "end": v(182.81, 623.62) * mm});
            skArc(sketch, "E401.MirrorCS", {"start": v(482.81, 583.62) * mm, "mid": v(469.53, 610.34) * mm, "end": v(442.81, 623.62) * mm});
            skLineSegment(sketch, "E402", {"start": v(122.81, 638.62) * mm, "end": v(122.81, 663.62) * mm});
            skLineSegment(sketch, "E403", {"start": v(122.81, 663.62) * mm, "end": v(502.81, 663.62) * mm});
            skLineSegment(sketch, "E404", {"start": v(502.81, 663.62) * mm, "end": v(502.81, 638.62) * mm});
            skCircle(sketch, "E405", {"center": v(132.81, 385.62) * mm, "radius": 2 * mm});
            skCircle(sketch, "E406", {"center": v(132.81, 473.62) * mm, "radius": 2 * mm});
            skCircle(sketch, "E407.MirrorC", {"center": v(132.81, 561.62) * mm, "radius": 2 * mm});
            skCircle(sketch, "E408.MirrorC", {"center": v(492.81, 385.89) * mm, "radius": 2 * mm});
            skCircle(sketch, "E409.MirrorC", {"center": v(492.81, 473.62) * mm, "radius": 2 * mm});
            skCircle(sketch, "E410.MirrorC", {"center": v(492.81, 473.89) * mm, "radius": 2 * mm});
            skCircle(sketch, "E411.MirrorC", {"center": v(492.81, 561.89) * mm, "radius": 2 * mm});
            skLineSegment(sketch, "E412.trimOffspring", {"start": v(442.81, 643.62) * mm, "end": v(497.81, 643.62) * mm});
            skLineSegment(sketch, "E413", {"start": v(127.81, 643.62) * mm, "end": v(182.81, 643.62) * mm});
            skCircle(sketch, "E414.MirrorC", {"center": v(492.81, 313.62) * mm, "radius": 2.5 * mm});
            skCircle(sketch, "E415.MirrorC", {"center": v(474, 313.62) * mm, "radius": 2 * mm});
            skCircle(sketch, "E416.MirrorC", {"center": v(492.81, 327.7) * mm, "radius": 2 * mm});
            skCircle(sketch, "E417.MirrorC", {"center": v(132.81, 614.62) * mm, "radius": 2 * mm});
            skCircle(sketch, "E418.MirrorC", {"center": v(132.81, 633.62) * mm, "radius": 2.5 * mm});
            skCircle(sketch, "E419.MirrorC", {"center": v(151.81, 633.62) * mm, "radius": 2 * mm});
            skCircle(sketch, "E420.MirrorC", {"center": v(132.81, 594.62) * mm, "radius": 2 * mm});
            skCircle(sketch, "E421.MirrorC", {"center": v(474, 633.62) * mm, "radius": 2 * mm});
            skCircle(sketch, "E422.MirrorC", {"center": v(493, 614.62) * mm, "radius": 2 * mm});
            skCircle(sketch, "E423.MirrorC", {"center": v(493, 633.62) * mm, "radius": 2.5 * mm});
            skCircle(sketch, "E424.MirrorC", {"center": v(492.81, 347.7) * mm, "radius": 2 * mm});
            skCircle(sketch, "E425.MirrorC", {"center": v(454, 313.62) * mm, "radius": 2 * mm});
            skCircle(sketch, "E426.MirrorC", {"center": v(492.81, 594.62) * mm, "radius": 2 * mm});
            skCircle(sketch, "E427.MirrorC", {"center": v(454, 633.62) * mm, "radius": 2 * mm});
            skCircle(sketch, "E428.MirrorC", {"center": v(171.81, 633.62) * mm, "radius": 2 * mm});
            skLineSegment(sketch, "E429", {"start": v(122.81, 363.62) * mm, "end": v(142.81, 363.62) * mm});
            skLineSegment(sketch, "E430", {"start": v(182.81, 323.62) * mm, "end": v(182.81, 303.62) * mm});
            skLineSegment(sketch, "E431", {"start": v(142.81, 583.62) * mm, "end": v(122.81, 583.62) * mm});
            skLineSegment(sketch, "E432", {"start": v(182.81, 623.62) * mm, "end": v(182.81, 643.62) * mm});
            skLineSegment(sketch, "E433", {"start": v(442.81, 303.62) * mm, "end": v(442.81, 323.62) * mm});
            skLineSegment(sketch, "E434", {"start": v(482.81, 363.62) * mm, "end": v(502.81, 363.62) * mm});
            skLineSegment(sketch, "E435", {"start": v(442.81, 643.62) * mm, "end": v(442.81, 623.62) * mm});
            skLineSegment(sketch, "E436", {"start": v(482.81, 583.62) * mm, "end": v(502.81, 583.62) * mm});
            skLineSegment(sketch, "E437", {"start": v(502.81, 308.62) * mm, "end": v(502.81, 259.62) * mm});
            skLineSegment(sketch, "E438", {"start": v(502.81, 259.62) * mm, "end": v(122.81, 259.62) * mm});
            skLineSegment(sketch, "E439", {"start": v(122.81, 259.62) * mm, "end": v(122.81, 303.62) * mm});
            skPoint(sketch, "E440.visualSharp", {"position": v(502.81, 303.62) * mm});
            skArc(sketch, "E440.filletArc", {"start": v(497.81, 303.62) * mm, "mid": v(501.35, 305.09) * mm, "end": v(502.81, 308.62) * mm});
            skPoint(sketch, "E441.visualSharp", {"position": v(502.81, 643.62) * mm});
            skArc(sketch, "E441.filletArc", {"start": v(502.81, 638.62) * mm, "mid": v(501.35, 642.16) * mm, "end": v(497.81, 643.62) * mm});
            skPoint(sketch, "E442.visualSharp", {"position": v(122.81, 643.62) * mm});
            skArc(sketch, "E442.filletArc", {"start": v(127.81, 643.62) * mm, "mid": v(124.28, 642.16) * mm, "end": v(122.81, 638.62) * mm});
            skCircle(sketch, "E443", {"center": v(312.81, 633.62) * mm, "radius": 2 * mm});
            skCircle(sketch, "E444", {"center": v(312.81, 313.62) * mm, "radius": 2 * mm});
            skSolve(sketch);
        }
        {
            var Q0;
            {var subQ4=sQuery(id+"F16.wireOp",EDGE,"82c73330-30ee-4ce0-b7ae-c76676e96766");Q0=makeQuery(id+"F16.imprint","IMPRINT",FACE,{"disambiguationData":[TD([[makeQuery(id+"F16.imprint","IMPRINT",EDGE,{"derivedFrom":subQ4}),-1.0]])]});}
            var Q1;
            {var subQ1=sQuery(id+"F16.wireOp",EDGE,"c2653ec2-6f1e-43d4-b090-25398699ef070.MirrorCS");Q1=makeQuery(id+"F16.imprint","IMPRINT",FACE,{"disambiguationData":[TD([[makeQuery(id+"F16.imprint","IMPRINT",EDGE,{"derivedFrom":subQ1}),1.0]])]});}
            var Q2;
            {var subQ3=sQuery(id+"F16.wireOp",EDGE,"E402");Q2=makeQuery(id+"F16.imprint","IMPRINT",FACE,{"disambiguationData":[TD([[makeQuery(id+"F16.imprint","IMPRINT",EDGE,{"derivedFrom":subQ3}),-1.0]])]});}
            var Q3;
            Q3=makeQuery(id+"F16.imprint","IMPRINT",FACE,{"disambiguationData":[TD([[makeQuery(id+"F16.imprint","IMPRINT",EDGE,{"derivedFrom":sQuery(id+"F16.wireOp",EDGE,"E401.MirrorCS")}),1.0]])]});
            var Q4;
            Q4=makeQuery(id+"F16.imprint","IMPRINT",FACE,{"disambiguationData":[TD([[makeQuery(id+"F16.imprint","IMPRINT",EDGE,{"derivedFrom":sQuery(id+"F16.wireOp",EDGE,"E399.MirrorCS")}),-1.0]])]});
            var Q5;
            {var subQ1=sQuery(id+"F16.wireOp",EDGE,"E437");Q5=makeQuery(id+"F16.imprint","IMPRINT",FACE,{"disambiguationData":[TD([[makeQuery(id+"F16.imprint","IMPRINT",EDGE,{"derivedFrom":subQ1}),-1.0]])]});}
            extrude(context, id + "F17", {"entities" : qUnion([Q0, Q1, Q2, Q3, Q4, Q5]), "depth" : 4 * mm});
        }
        {
            var Q0;
            Q0=qCreatedBy(makeId("Top.planeOp"),FACE);
            var sketch = newSketch(context, id + "F18", { "sketchPlane" : qUnion([Q0])});
            skLineSegment(sketch, "E445.bottom", {"start": v(911.53, 540.54) * mm, "end": v(966.53, 540.54) * mm});
            skLineSegment(sketch, "E445.left", {"start": v(906.53, 545.54) * mm, "end": v(906.53, 600.54) * mm});
            skPoint(sketch, "E446", {"position": v(906.53, 555.54) * mm});
            skPoint(sketch, "E447", {"position": v(921.53, 600.54) * mm});
            skCircle(sketch, "E448", {"center": v(935.53, 550.54) * mm, "radius": 2 * mm});
            skPoint(sketch, "E449.visualSharp", {"position": v(906.53, 540.54) * mm});
            skArc(sketch, "E449.filletArc", {"start": v(906.53, 545.54) * mm, "mid": v(908, 542) * mm, "end": v(911.53, 540.54) * mm});
            skCircle(sketch, "E450", {"center": v(916.53, 550.54) * mm, "radius": 2.5 * mm});
            skLineSegment(sketch, "E451", {"start": v(906.53, 540.54) * mm, "end": v(1281.53, 540.54) * mm});
            skLineSegment(sketch, "E452", {"start": v(1286.53, 545.54) * mm, "end": v(1286.53, 915.54) * mm});
            skLineSegment(sketch, "E453", {"start": v(906.53, 540.54) * mm, "end": v(906.53, 915.54) * mm});
            skLineSegment(sketch, "E454", {"start": v(1281.53, 920.54) * mm, "end": v(911.53, 920.54) * mm});
            skCircle(sketch, "E455.MirrorC", {"center": v(1276.53, 550.54) * mm, "radius": 2.5 * mm});
            skCircle(sketch, "E456.MirrorC", {"center": v(1257.53, 550.54) * mm, "radius": 2 * mm});
            skCircle(sketch, "E457.MirrorC", {"center": v(916.53, 910.54) * mm, "radius": 2.5 * mm});
            skCircle(sketch, "E458.MirrorC", {"center": v(1271.53, 910.55) * mm, "radius": 2.5 * mm});
            skPoint(sketch, "E459", {"position": v(926.53, 540.54) * mm});
            skPoint(sketch, "E460.orphan", {"position": v(1096.53, 540.54) * mm});
            skLineSegment(sketch, "E461.trimOffspring", {"start": v(1096.53, 905.54) * mm, "end": v(1271.53, 905.54) * mm});
            skPoint(sketch, "E462.MirrorCS.start.orphan", {"position": v(901.53, 900.55) * mm});
            skLineSegment(sketch, "E463.trimOffspring", {"start": v(1271.53, 730.54) * mm, "end": v(1271.53, 905.54) * mm});
            skPoint(sketch, "E464.MirrorCS.start.orphan", {"position": v(1266.53, 540.54) * mm});
            skPoint(sketch, "E465.trimOffspring.end.orphan", {"position": v(921.53, 920.54) * mm});
            skPoint(sketch, "E466.orphan", {"position": v(1271.53, 920.54) * mm});
            skPoint(sketch, "E467.trimOffspring.end.orphan", {"position": v(1281.53, 900.55) * mm});
            skPoint(sketch, "E468.MirrorCS.start.orphan", {"position": v(1286.53, 555.54) * mm});
            skPoint(sketch, "E469.trimOffspring.end.orphan", {"position": v(1286.53, 560.55) * mm});
            skPoint(sketch, "E470.trimOffspring.end.orphan", {"position": v(906.53, 560.55) * mm});
            skPoint(sketch, "E471.orphan", {"position": v(1286.53, 730.54) * mm});
            skPoint(sketch, "E472.orphan", {"position": v(1281.53, 730.54) * mm});
            skPoint(sketch, "E473.orphan", {"position": v(906.53, 730.54) * mm});
            skPoint(sketch, "E474.orphan", {"position": v(1096.53, 920.54) * mm});
            skPoint(sketch, "E475.visualSharp", {"position": v(1286.53, 920.54) * mm});
            skArc(sketch, "E475.filletArc", {"start": v(1286.53, 915.54) * mm, "mid": v(1285.07, 919.08) * mm, "end": v(1281.53, 920.54) * mm});
            skPoint(sketch, "E476.visualSharp", {"position": v(906.53, 920.54) * mm});
            skArc(sketch, "E476.filletArc", {"start": v(911.53, 920.54) * mm, "mid": v(908, 919.08) * mm, "end": v(906.53, 915.54) * mm});
            skPoint(sketch, "E477.visualSharp", {"position": v(1286.53, 540.54) * mm});
            skArc(sketch, "E477.filletArc", {"start": v(1281.53, 540.54) * mm, "mid": v(1285.07, 542) * mm, "end": v(1286.53, 545.54) * mm});
            skPoint(sketch, "E478.end.orphan", {"position": v(-182644023.01, 555.54) * mm});
            skPoint(sketch, "E479.trimOffspring.start.orphan", {"position": v(1271.53, 600.54) * mm});
            skPoint(sketch, "E480.trimOffspring.start.orphan", {"position": v(182646216.07, 555.54) * mm});
            skPoint(sketch, "E481.orphan", {"position": v(182646216.07, 895.54) * mm});
            skPoint(sketch, "E482.trimOffspring.end.orphan", {"position": v(921.53, 860.55) * mm});
            skPoint(sketch, "E483.orphan", {"position": v(-182644023.01, 915.54) * mm});
            skLineSegment(sketch, "E484.MirrorCS", {"start": v(921.53, 730.54) * mm, "end": v(921.53, 905.54) * mm});
            skLineSegment(sketch, "E485.MirrorCS", {"start": v(1096.53, 905.54) * mm, "end": v(921.53, 905.54) * mm});
            skLineSegment(sketch, "E486.MirrorCS", {"start": v(1271.53, 730.54) * mm, "end": v(1271.53, 555.54) * mm});
            skLineSegment(sketch, "E487.MirrorCS", {"start": v(1096.53, 555.54) * mm, "end": v(1271.53, 555.54) * mm});
            skLineSegment(sketch, "E488.MirrorCS", {"start": v(1096.53, 555.54) * mm, "end": v(921.53, 555.54) * mm});
            skLineSegment(sketch, "E489.MirrorCS", {"start": v(921.53, 730.54) * mm, "end": v(921.53, 555.54) * mm});
            skLineSegment(sketch, "E490.0", {"start": v(926.53, 730.54) * mm, "end": v(926.53, 560.54) * mm});
            skLineSegment(sketch, "E490.1", {"start": v(1096.53, 560.54) * mm, "end": v(926.53, 560.54) * mm});
            skLineSegment(sketch, "E490.2", {"start": v(926.53, 730.54) * mm, "end": v(926.53, 900.54) * mm});
            skLineSegment(sketch, "E490.3", {"start": v(1096.53, 560.54) * mm, "end": v(1266.53, 560.54) * mm});
            skLineSegment(sketch, "E490.4", {"start": v(1096.53, 900.54) * mm, "end": v(926.53, 900.54) * mm});
            skLineSegment(sketch, "E490.5", {"start": v(1096.53, 900.54) * mm, "end": v(1266.53, 900.54) * mm});
            skLineSegment(sketch, "E490.6", {"start": v(1266.53, 730.54) * mm, "end": v(1266.53, 900.54) * mm});
            skLineSegment(sketch, "E490.7", {"start": v(1266.53, 730.54) * mm, "end": v(1266.53, 560.54) * mm});
            skSolve(sketch);
        }
        {
            var Q0;
            {var subQ6=sQuery(id+"F18.wireOp",EDGE,"E478");Q0=makeQuery(id+"F18.imprint","IMPRINT",FACE,{"disambiguationData":[TD([[makeQuery(id+"F18.imprint","IMPRINT",EDGE,{"derivedFrom":subQ6}),-1.0]])]});}
            var Q1;
            Q1=makeQuery(id+"F18.imprint","IMPRINT",FACE,{"disambiguationData":[TD([[makeQuery(id+"F18.imprint","IMPRINT",EDGE,{"derivedFrom":sQuery(id+"F18.wireOp",EDGE,"E448")}),-1.0]])]});
            var Q2;
            Q2=makeQuery(id+"F18.imprint","IMPRINT",FACE,{"disambiguationData":[TD([[makeQuery(id+"F18.imprint","IMPRINT",EDGE,{"derivedFrom":sQuery(id+"F18.wireOp",EDGE,"E461.trimOffspring")}),-1.0]])]});
            extrude(context, id + "F19", {"entities" : qUnion([Q0, Q1, Q2]), "depth" : 4 * mm});
        }
        {
            var Q0;
            Q0=makeQuery(id+"F17.opExtrude","CAP_FACE",FACE,{"disambiguationData":[OSD([sQuery(id+"F16.wireOp",EDGE,"82c73330-30ee-4ce0-b7ae-c76676e96766"),sQuery(id+"F16.wireOp",EDGE,"6159bdec-8f67-48df-ada1-b633f0472b5d"),sQuery(id+"F16.wireOp",EDGE,"E389"),sQuery(id+"F16.wireOp",EDGE,"E396"),sQuery(id+"F16.wireOp",EDGE,"64241ade-e88b-4d53-8ac9-28b0a5b8250c"),sQuery(id+"F16.wireOp",EDGE,"E397"),sQuery(id+"F16.wireOp",EDGE,"E398"),sQuery(id+"F16.wireOp",EDGE,"E399.MirrorCS"),sQuery(id+"F16.wireOp",EDGE,"753134ca-0ba6-43d0-a89f-bc8703a781450.MirrorCS"),sQuery(id+"F16.wireOp",EDGE,"d855c492-912a-4833-a90a-e979491345e50.MirrorCS"),sQuery(id+"F16.wireOp",EDGE,"c2653ec2-6f1e-43d4-b090-25398699ef070.MirrorCS"),sQuery(id+"F16.wireOp",EDGE,"E400.MirrorCS"),sQuery(id+"F16.wireOp",EDGE,"0665624d-8878-4a35-bb48-829bd46e2ff50.MirrorCS"),sQuery(id+"F16.wireOp",EDGE,"E401.MirrorCS"),sQuery(id+"F16.wireOp",EDGE,"e0f5842c-4877-4b24-b5c6-21cafd525e700.MirrorCS"),sQuery(id+"F16.wireOp",EDGE,"adf0b613-69af-4113-90ba-ee4a629042250.MirrorCS"),sQuery(id+"F16.wireOp",EDGE,"E402"),sQuery(id+"F16.wireOp",EDGE,"E403"),sQuery(id+"F16.wireOp",EDGE,"E404")])],"isStart":false});
            var sketch = newSketch(context, id + "F20", { "sketchPlane" : qUnion([Q0])});
            skPoint(sketch, "E491.visualSharp", {"position": v(-437.48, 591.17) * mm});
            skLineSegment(sketch, "E492", {"start": v(-437.48, 596.17) * mm, "end": v(-437.48, 872.33) * mm});
            skLineSegment(sketch, "E493", {"start": v(-57.48, 926) * mm, "end": v(-57.48, 596.17) * mm});
            skLineSegment(sketch, "E494", {"start": v(-62.48, 591.17) * mm, "end": v(-432.48, 591.17) * mm});
            skArc(sketch, "E495.MirrorCS", {"start": v(-77.54, 651.17) * mm, "mid": v(-90.77, 624.35) * mm, "end": v(-117.54, 611) * mm});
            skArc(sketch, "E496.MirrorCS", {"start": v(-417.48, 872.33) * mm, "mid": v(-403.58, 897.65) * mm, "end": v(-377.48, 910.02) * mm});
            skArc(sketch, "E497.MirrorCS", {"start": v(-77.48, 871) * mm, "mid": v(-90.76, 897.7) * mm, "end": v(-117.48, 911) * mm});
            skLineSegment(sketch, "E498", {"start": v(-164.87, 951.17) * mm, "end": v(-57.48, 951.17) * mm});
            skLineSegment(sketch, "E499", {"start": v(-57.48, 951.17) * mm, "end": v(-57.48, 931) * mm});
            skLineSegment(sketch, "E500", {"start": v(-373.35, 931.18) * mm, "end": v(-373.35, 935.17) * mm});
            skLineSegment(sketch, "E501", {"start": v(-373.35, 935.17) * mm, "end": v(-330.35, 935.17) * mm});
            skLineSegment(sketch, "E502", {"start": v(-330.35, 935.17) * mm, "end": v(-330.35, 931.17) * mm});
            skPoint(sketch, "E503.MirrorCS.start.orphan", {"position": v(-117.48, 931) * mm});
            skLineSegment(sketch, "E504.MirrorCS", {"start": v(-164.3, 935.17) * mm, "end": v(-164.3, 931.17) * mm});
            skLineSegment(sketch, "E505.MirrorCS", {"start": v(-121.3, 935.17) * mm, "end": v(-164.3, 935.17) * mm});
            skLineSegment(sketch, "E506.MirrorCS", {"start": v(-121.3, 931.17) * mm, "end": v(-121.3, 935.17) * mm});
            skCircle(sketch, "E507.MirrorC", {"center": v(-427.66, 902.17) * mm, "radius": 2 * mm});
            skCircle(sketch, "E508.MirrorC", {"center": v(-427.66, 921.17) * mm, "radius": 2.5 * mm});
            skCircle(sketch, "E509.MirrorC", {"center": v(-408.66, 921.17) * mm, "radius": 2 * mm});
            skCircle(sketch, "E510.MirrorC", {"center": v(-427.42, 882.18) * mm, "radius": 2 * mm});
            skCircle(sketch, "E511.MirrorC", {"center": v(-388.66, 921.17) * mm, "radius": 2 * mm});
            skCircle(sketch, "E512", {"center": v(-427.48, 761.17) * mm, "radius": 2 * mm});
            skCircle(sketch, "E513", {"center": v(-427.48, 673.17) * mm, "radius": 2 * mm});
            skCircle(sketch, "E514.MirrorC", {"center": v(-427.48, 849.17) * mm, "radius": 2 * mm});
            skCircle(sketch, "E515.MirrorC", {"center": v(-67.48, 673.17) * mm, "radius": 2 * mm});
            skCircle(sketch, "E516.MirrorC", {"center": v(-67.48, 761.17) * mm, "radius": 2 * mm});
            skCircle(sketch, "E517.MirrorC", {"center": v(-67.48, 849.17) * mm, "radius": 2 * mm});
            skCircle(sketch, "E518.MirrorC", {"center": v(-67.54, 620.17) * mm, "radius": 2 * mm});
            skCircle(sketch, "E519.MirrorC", {"center": v(-67.3, 601.17) * mm, "radius": 2.5 * mm});
            skCircle(sketch, "E520.MirrorC", {"center": v(-86.3, 601.17) * mm, "radius": 2 * mm});
            skCircle(sketch, "E521.MirrorC", {"center": v(-106.3, 601.17) * mm, "radius": 2 * mm});
            skCircle(sketch, "E522.MirrorC", {"center": v(-67.48, 882.17) * mm, "radius": 2 * mm});
            skCircle(sketch, "E523.MirrorC", {"center": v(-67.48, 902.17) * mm, "radius": 2 * mm});
            skCircle(sketch, "E524.MirrorC", {"center": v(-67.48, 921.17) * mm, "radius": 2.5 * mm});
            skCircle(sketch, "E525.MirrorC", {"center": v(-86.48, 921.17) * mm, "radius": 2 * mm});
            skCircle(sketch, "E526.MirrorC", {"center": v(-106.48, 921.17) * mm, "radius": 2 * mm});
            skLineSegment(sketch, "E527.trimOffspring", {"start": v(-117.48, 931) * mm, "end": v(-62.48, 931) * mm});
            skLineSegment(sketch, "E528", {"start": v(-117.48, 591) * mm, "end": v(-117.54, 611) * mm});
            skLineSegment(sketch, "E529", {"start": v(-117.48, 911) * mm, "end": v(-117.48, 931) * mm});
            skLineSegment(sketch, "E530", {"start": v(-77.48, 871) * mm, "end": v(-57.48, 871) * mm});
            skCircle(sketch, "E531", {"center": v(-421, 1024.4) * mm, "radius": 1.5 * mm});
            skCircle(sketch, "E532", {"center": v(-421.18, 974.46) * mm, "radius": 1.5 * mm});
            skCircle(sketch, "E533", {"center": v(-276, 974.46) * mm, "radius": 1.5 * mm});
            skCircle(sketch, "E534", {"center": v(-276, 1024.46) * mm, "radius": 1.5 * mm});
            skLineSegment(sketch, "E535", {"start": v(-437.48, 951.17) * mm, "end": v(-437.48, 1028.35) * mm});
            skLineSegment(sketch, "E536", {"start": v(-432.48, 1033.35) * mm, "end": v(-268.2, 1033.35) * mm});
            skArc(sketch, "E537", {"start": v(-263.94, 1030.98) * mm, "mid": v(-221.2, 982.64) * mm, "end": v(-164.87, 951.17) * mm});
            skPoint(sketch, "E538.visualSharp", {"position": v(-437.48, 1033.35) * mm});
            skArc(sketch, "E538.filletArc", {"start": v(-432.48, 1033.35) * mm, "mid": v(-436.01, 1031.89) * mm, "end": v(-437.48, 1028.35) * mm});
            skPoint(sketch, "E539.visualSharp", {"position": v(-265.39, 1033.35) * mm});
            skArc(sketch, "E539.filletArc", {"start": v(-263.94, 1030.98) * mm, "mid": v(-265.76, 1032.72) * mm, "end": v(-268.2, 1033.35) * mm});
            skCircle(sketch, "E540", {"center": v(-270.3, 766.4) * mm, "radius": 1.5 * mm});
            skCircle(sketch, "E541", {"center": v(-222.48, 773.77) * mm, "radius": 1.5 * mm});
            skCircle(sketch, "E542", {"center": v(-222.58, 847.1) * mm, "radius": 1.5 * mm});
            skCircle(sketch, "E543", {"center": v(-270.6, 847.1) * mm, "radius": 1.5 * mm});
            skLineSegment(sketch, "E544.top", {"start": v(-330.35, 891.17) * mm, "end": v(-373.35, 891.17) * mm});
            skLineSegment(sketch, "E544.left", {"start": v(-330.35, 931.17) * mm, "end": v(-330.35, 891.17) * mm});
            skLineSegment(sketch, "E545", {"start": v(-373.35, 931.18) * mm, "end": v(-373.35, 891.17) * mm});
            skLineSegment(sketch, "E546.MirrorCS", {"start": v(-164.3, 931.17) * mm, "end": v(-164.3, 891.17) * mm});
            skLineSegment(sketch, "E547.MirrorCS", {"start": v(-164.3, 891.17) * mm, "end": v(-122.04, 891.17) * mm});
            skLineSegment(sketch, "E548.MirrorCS", {"start": v(-121.3, 931.17) * mm, "end": v(-122.04, 891.17) * mm});
            skLineSegment(sketch, "E549", {"start": v(-437.48, 930.02) * mm, "end": v(-437.48, 951.17) * mm});
            skLineSegment(sketch, "E550", {"start": v(-377.49, 930.02) * mm, "end": v(-432.48, 930.02) * mm});
            skLineSegment(sketch, "E551", {"start": v(-417.48, 872.33) * mm, "end": v(-437.48, 872.33) * mm});
            skLineSegment(sketch, "E552", {"start": v(-377.48, 910.02) * mm, "end": v(-377.49, 930.02) * mm});
            skLineSegment(sketch, "E553", {"start": v(-437.48, 872.33) * mm, "end": v(-437.48, 925.02) * mm});
            skCircle(sketch, "E554", {"center": v(-247.48, 943.17) * mm, "radius": 3 * mm});
            skPoint(sketch, "E555.visualSharp", {"position": v(-698.98, 819.12) * mm});
            skPoint(sketch, "E556.visualSharp", {"position": v(-604.02, 688.54) * mm});
            skLineSegment(sketch, "E557.left", {"start": v(-604.02, 693.54) * mm, "end": v(-604.02, 814.12) * mm});
            skPoint(sketch, "E558.visualSharp", {"position": v(-604.02, 819.12) * mm});
            skLineSegment(sketch, "E557.bottom", {"start": v(-609.02, 688.54) * mm, "end": v(-693.98, 688.54) * mm});
            skLineSegment(sketch, "E557.top", {"start": v(-609.02, 819.12) * mm, "end": v(-693.98, 819.12) * mm});
            skCircle(sketch, "E559", {"center": v(-693.98, 693.54) * mm, "radius": 1.5 * mm});
            skArc(sketch, "E558.filletArc", {"start": v(-604.02, 814.12) * mm, "mid": v(-605.48, 817.65) * mm, "end": v(-609.02, 819.12) * mm});
            skCircle(sketch, "E560", {"center": v(-609.02, 814.12) * mm, "radius": 1.5 * mm});
            skArc(sketch, "E556.filletArc", {"start": v(-609.02, 688.54) * mm, "mid": v(-605.48, 690) * mm, "end": v(-604.02, 693.54) * mm});
            skCircle(sketch, "E561", {"center": v(-609.02, 693.54) * mm, "radius": 1.5 * mm});
            skArc(sketch, "E555.filletArc", {"start": v(-693.98, 819.12) * mm, "mid": v(-697.52, 817.65) * mm, "end": v(-698.98, 814.12) * mm});
            skCircle(sketch, "E562", {"center": v(-693.98, 814.12) * mm, "radius": 1.5 * mm});
            skLineSegment(sketch, "E557.right", {"start": v(-698.98, 693.54) * mm, "end": v(-698.98, 814.12) * mm});
            skArc(sketch, "E563.filletArc", {"start": v(-698.98, 693.54) * mm, "mid": v(-697.52, 690) * mm, "end": v(-693.98, 688.54) * mm});
            skCircle(sketch, "E564", {"center": v(-288.73, 868.53) * mm, "radius": 1.5 * mm});
            skCircle(sketch, "E565", {"center": v(-203.77, 868.53) * mm, "radius": 1.5 * mm});
            skCircle(sketch, "E566", {"center": v(-203.77, 747.95) * mm, "radius": 1.5 * mm});
            skCircle(sketch, "E567", {"center": v(-288.73, 747.95) * mm, "radius": 1.5 * mm});
            skLineSegment(sketch, "E568", {"start": v(-433.47, 941.17) * mm, "end": v(-388.66, 941.17) * mm});
            skLineSegment(sketch, "E569", {"start": v(-388.66, 941.17) * mm, "end": v(-388.66, 951.17) * mm});
            skLineSegment(sketch, "E570", {"start": v(-433.47, 951.17) * mm, "end": v(-388.66, 951.17) * mm});
            skLineSegment(sketch, "E571", {"start": v(-433.47, 941.17) * mm, "end": v(-433.47, 951.17) * mm});
            skLineSegment(sketch, "E572.MirrorCS", {"start": v(-106.3, 941.17) * mm, "end": v(-106.3, 951.17) * mm});
            skLineSegment(sketch, "E573.MirrorCS", {"start": v(-61.48, 941.17) * mm, "end": v(-106.3, 941.17) * mm});
            skLineSegment(sketch, "E574.MirrorCS", {"start": v(-61.48, 951.17) * mm, "end": v(-106.3, 951.17) * mm});
            skLineSegment(sketch, "E575.MirrorCS", {"start": v(-61.48, 941.17) * mm, "end": v(-61.48, 951.17) * mm});
            skPoint(sketch, "E576.left.start.orphan", {"position": v(-651.5, 753.83) * mm});
            skPoint(sketch, "E577.start.orphan", {"position": v(-651.5, 688.54) * mm});
            skPoint(sketch, "E578.trimOffspring.end.orphan", {"position": v(-651.5, 819.12) * mm});
            skCircle(sketch, "E579", {"center": v(-667.5, 737.83) * mm, "radius": 1.5 * mm});
            skCircle(sketch, "E580", {"center": v(-667.5, 769.83) * mm, "radius": 1.5 * mm});
            skCircle(sketch, "E581", {"center": v(-635.6, 769.88) * mm, "radius": 1.5 * mm});
            skCircle(sketch, "E582", {"center": v(-635.5, 737.83) * mm, "radius": 1.5 * mm});
            skCircle(sketch, "E583", {"center": v(-651.5, 753.83) * mm, "radius": 2.21 * mm});
            skLineSegment(sketch, "E584.trimOffspring", {"start": v(-635.6, 769.83) * mm, "end": v(-635.5, 769.83) * mm});
            skArc(sketch, "E585.trimOffspring", {"start": v(-635.6, 769.83) * mm, "mid": v(-635.6, 769.85) * mm, "end": v(-635.6, 769.88) * mm});
            skCircle(sketch, "E586.1.0.0", {"center": v(-646.3, 753.83) * mm, "radius": 2.21 * mm});
            skCircle(sketch, "E586.2.0.0", {"center": v(-641.1, 753.83) * mm, "radius": 2.21 * mm});
            skCircle(sketch, "E586.3.0.0", {"center": v(-635.9, 753.83) * mm, "radius": 2.21 * mm});
            skLineSegment(sketch, "E586.direction1", {"start": v(-651.5, 753.83) * mm, "end": v(-646.3, 753.83) * mm, "construction": true});
            skCircle(sketch, "E587.1.0.0", {"center": v(-645.63, 748) * mm, "radius": 2.21 * mm});
            skCircle(sketch, "E587.2.0.0", {"center": v(-639.76, 742.18) * mm, "radius": 2.21 * mm});
            skLineSegment(sketch, "E587.direction1", {"start": v(-651.5, 753.83) * mm, "end": v(-645.63, 748) * mm, "construction": true});
            skCircle(sketch, "E588.1.0.0", {"center": v(-651.49, 748.85) * mm, "radius": 2.21 * mm});
            skCircle(sketch, "E588.2.0.0", {"center": v(-651.47, 743.86) * mm, "radius": 2.21 * mm});
            skCircle(sketch, "E588.3.0.0", {"center": v(-651.46, 738.88) * mm, "radius": 2.21 * mm});
            skLineSegment(sketch, "E588.direction1", {"start": v(-651.5, 753.83) * mm, "end": v(-651.49, 748.85) * mm, "construction": true});
            skCircle(sketch, "E589.MirrorC", {"center": v(-651.49, 758.81) * mm, "radius": 2.21 * mm});
            skCircle(sketch, "E590.MirrorC", {"center": v(-651.47, 763.8) * mm, "radius": 2.21 * mm});
            skCircle(sketch, "E591.MirrorC", {"center": v(-651.46, 768.78) * mm, "radius": 2.21 * mm});
            skCircle(sketch, "E592.MirrorC", {"center": v(-645.63, 759.66) * mm, "radius": 2.21 * mm});
            skCircle(sketch, "E593.MirrorC", {"center": v(-639.76, 765.48) * mm, "radius": 2.21 * mm});
            skCircle(sketch, "E594.MirrorC", {"center": v(-657.34, 747.97) * mm, "radius": 2.21 * mm});
            skCircle(sketch, "E595.MirrorC", {"center": v(-656.7, 753.8) * mm, "radius": 2.21 * mm});
            skCircle(sketch, "E596.MirrorC", {"center": v(-657.4, 759.62) * mm, "radius": 2.21 * mm});
            skCircle(sketch, "E597.MirrorC", {"center": v(-661.9, 753.77) * mm, "radius": 2.21 * mm});
            skCircle(sketch, "E598.MirrorC", {"center": v(-663.17, 742.11) * mm, "radius": 2.21 * mm});
            skCircle(sketch, "E599.MirrorC", {"center": v(-663.3, 765.42) * mm, "radius": 2.21 * mm});
            skCircle(sketch, "E600.MirrorC", {"center": v(-667.1, 753.74) * mm, "radius": 2.21 * mm});
            skCircle(sketch, "E601", {"center": v(-67.54, 640.17) * mm, "radius": 2 * mm});
            skCircle(sketch, "E602.MirrorC", {"center": v(-286.48, 995.97) * mm, "radius": 10 * mm});
            skArc(sketch, "E603.MirrorCS", {"start": v(-417.42, 651) * mm, "mid": v(-404.13, 624.28) * mm, "end": v(-377.42, 611) * mm});
            skLineSegment(sketch, "E604.MirrorCS", {"start": v(-377.48, 591) * mm, "end": v(-377.42, 611) * mm});
            skLineSegment(sketch, "E605", {"start": v(-417.42, 651) * mm, "end": v(-437.48, 651) * mm});
            skLineSegment(sketch, "E606", {"start": v(-77.54, 651.17) * mm, "end": v(-57.48, 651.17) * mm});
            skCircle(sketch, "E607.MirrorC", {"center": v(-388.66, 601.17) * mm, "radius": 2 * mm});
            skCircle(sketch, "E608.MirrorC", {"center": v(-427.66, 601.17) * mm, "radius": 2.5 * mm});
            skCircle(sketch, "E609.MirrorC", {"center": v(-427.42, 620.17) * mm, "radius": 2 * mm});
            skCircle(sketch, "E610.MirrorC", {"center": v(-427.42, 640.17) * mm, "radius": 2 * mm});
            skCircle(sketch, "E611.MirrorC", {"center": v(-408.66, 601.17) * mm, "radius": 2 * mm});
            skCircle(sketch, "E612", {"center": v(-247.48, 601.17) * mm, "radius": 2 * mm});
            skArc(sketch, "E613.filletArc", {"start": v(-437.48, 596.17) * mm, "mid": v(-436.01, 592.64) * mm, "end": v(-432.48, 591.17) * mm});
            skPoint(sketch, "E614.visualSharp", {"position": v(-57.48, 591.17) * mm});
            skArc(sketch, "E614.filletArc", {"start": v(-62.48, 591.17) * mm, "mid": v(-58.94, 592.64) * mm, "end": v(-57.48, 596.17) * mm});
            skPoint(sketch, "E615.visualSharp", {"position": v(-57.48, 931) * mm});
            skArc(sketch, "E615.filletArc", {"start": v(-57.48, 926) * mm, "mid": v(-58.94, 929.53) * mm, "end": v(-62.48, 931) * mm});
            skPoint(sketch, "E616.visualSharp", {"position": v(-437.48, 930.02) * mm});
            skArc(sketch, "E616.filletArc", {"start": v(-432.48, 930.02) * mm, "mid": v(-436.01, 928.56) * mm, "end": v(-437.48, 925.02) * mm});
            skLineSegment(sketch, "E617", {"start": v(-437.48, 930.02) * mm, "end": v(-437.48, 925.02) * mm});
            skLineSegment(sketch, "E618", {"start": v(-57.48, 931) * mm, "end": v(-57.48, 926) * mm});
            skLineSegment(sketch, "E619.bottom", {"start": v(-409.9, 1013.6) * mm, "end": v(-311.77, 1013.6) * mm});
            skLineSegment(sketch, "E619.top", {"start": v(-409.9, 972.89) * mm, "end": v(-311.77, 972.89) * mm});
            skLineSegment(sketch, "E619.left", {"start": v(-409.9, 1013.6) * mm, "end": v(-409.9, 972.89) * mm});
            skLineSegment(sketch, "E619.right", {"start": v(-311.77, 1013.6) * mm, "end": v(-311.77, 972.89) * mm});
            skLineSegment(sketch, "E620.bottom", {"start": v(-1331.98, 846.7) * mm, "end": v(-1233.84, 846.7) * mm});
            skLineSegment(sketch, "E620.top", {"start": v(-1331.98, 805.99) * mm, "end": v(-1233.84, 805.99) * mm});
            skPoint(sketch, "E621.visualSharp", {"position": v(-1359.55, 866.45) * mm});
            skPoint(sketch, "E622.visualSharp", {"position": v(-1187.46, 866.45) * mm});
            skLineSegment(sketch, "E623", {"start": v(-1359.55, 424.28) * mm, "end": v(-1359.55, 861.45) * mm});
            skLineSegment(sketch, "E624", {"start": v(-1354.55, 866.45) * mm, "end": v(-1192.46, 866.45) * mm});
            skCircle(sketch, "E625", {"center": v(-1250.66, 605.61) * mm, "radius": 1.5 * mm});
            skCircle(sketch, "E626.MirrorC", {"center": v(-1208.56, 829.07) * mm, "radius": 10 * mm});
            skCircle(sketch, "E627", {"center": v(-1231.94, 700.37) * mm, "radius": 1.5 * mm});
            skCircle(sketch, "E628", {"center": v(-1198.08, 807.56) * mm, "radius": 1.5 * mm});
            skCircle(sketch, "E629", {"center": v(-1231.94, 579.79) * mm, "radius": 1.5 * mm});
            skCircle(sketch, "E630", {"center": v(-1250.75, 678.95) * mm, "radius": 1.5 * mm});
            skCircle(sketch, "E631", {"center": v(-1316.9, 700.37) * mm, "radius": 1.5 * mm});
            skCircle(sketch, "E632", {"center": v(-1298.78, 678.95) * mm, "radius": 1.5 * mm});
            skLineSegment(sketch, "E620.left", {"start": v(-1331.98, 846.7) * mm, "end": v(-1331.98, 805.99) * mm});
            skCircle(sketch, "E633", {"center": v(-1343.26, 807.56) * mm, "radius": 1.5 * mm});
            skLineSegment(sketch, "E620.right", {"start": v(-1233.84, 846.7) * mm, "end": v(-1233.84, 805.99) * mm});
            skCircle(sketch, "E634", {"center": v(-1343.08, 857.51) * mm, "radius": 1.5 * mm});
            skCircle(sketch, "E635", {"center": v(-1198.08, 857.56) * mm, "radius": 1.5 * mm});
            skLineSegment(sketch, "E636", {"start": v(-1187.46, 424.28) * mm, "end": v(-1359.55, 424.28) * mm});
            skLineSegment(sketch, "E637", {"start": v(-1187.46, 861.45) * mm, "end": v(-1187.46, 424.28) * mm});
            skCircle(sketch, "E638", {"center": v(-1316.82, 579.7) * mm, "radius": 1.5 * mm});
            skCircle(sketch, "E639", {"center": v(-1298.4, 598.14) * mm, "radius": 1.5 * mm});
            skArc(sketch, "E640.filletArc", {"start": v(-1187.46, 861.45) * mm, "mid": v(-1188.93, 864.99) * mm, "end": v(-1192.46, 866.45) * mm});
            skArc(sketch, "E641.filletArc", {"start": v(-1354.55, 866.45) * mm, "mid": v(-1358.09, 864.99) * mm, "end": v(-1359.55, 861.45) * mm});
            skCircle(sketch, "E642", {"center": v(-1273.5, 776.28) * mm, "radius": 3 * mm});
            skCircle(sketch, "E643", {"center": v(-1345.1, 754.28) * mm, "radius": 2 * mm});
            skCircle(sketch, "E644.MirrorC", {"center": v(-1201.92, 754.28) * mm, "radius": 2 * mm});
            skCircle(sketch, "E645.MirrorC", {"center": v(-1345.1, 434.28) * mm, "radius": 2 * mm});
            skCircle(sketch, "E646.MirrorC", {"center": v(-1201.92, 434.28) * mm, "radius": 2 * mm});
            skLineSegment(sketch, "E647.bottom", {"start": v(-1346.37, 861.24) * mm, "end": v(-1194.23, 861.24) * mm});
            skLineSegment(sketch, "E647.top", {"start": v(-1346.37, 793.18) * mm, "end": v(-1194.23, 793.18) * mm});
            skLineSegment(sketch, "E647.left", {"start": v(-1346.37, 861.24) * mm, "end": v(-1346.37, 793.18) * mm});
            skLineSegment(sketch, "E647.right", {"start": v(-1194.23, 861.24) * mm, "end": v(-1194.23, 793.18) * mm});
            skSolve(sketch);
        }
        {
            var Q0;
            {var subQ4=sQuery(id+"F20.wireOp",EDGE,"274de717-3da0-4c64-9ed4-fe21729b6c2f");Q0=makeQuery(id+"F20.imprint","IMPRINT",FACE,{"disambiguationData":[TD([[makeQuery(id+"F20.imprint","IMPRINT",EDGE,{"derivedFrom":subQ4}),-1.0]])]});}
            var Q1;
            Q1=makeQuery(id+"F20.imprint","IMPRINT",FACE,{"disambiguationData":[TD([[makeQuery(id+"F20.imprint","IMPRINT",EDGE,{"derivedFrom":sQuery(id+"F20.wireOp",EDGE,"E495.MirrorCS")}),-1.0]])]});
            var Q2;
            {var subQ4=sQuery(id+"F20.wireOp",EDGE,"1e5e7644-ac6b-445a-a06a-048c4de03991");Q2=makeQuery(id+"F20.imprint","IMPRINT",FACE,{"disambiguationData":[TD([[makeQuery(id+"F20.imprint","IMPRINT",EDGE,{"derivedFrom":subQ4}),-1.0]])]});}
            var Q3;
            {var subQ3=sQuery(id+"F20.wireOp",EDGE,"274de717-3da0-4c64-9ed4-fe21729b6c2f");Q3=makeQuery(id+"F20.imprint","IMPRINT",FACE,{"disambiguationData":[TD([[makeQuery(id+"F20.imprint","IMPRINT",EDGE,{"derivedFrom":subQ3}),-1.0]])]});}
            var Q4;
            Q4=makeQuery(id+"F20.imprint","IMPRINT",FACE,{"disambiguationData":[TD([[makeQuery(id+"F20.imprint","IMPRINT",EDGE,{"derivedFrom":sQuery(id+"F20.wireOp",EDGE,"E531")}),1.0]])]});
            var Q5;
            Q5=makeQuery(id+"F20.imprint","IMPRINT",FACE,{"disambiguationData":[TD([[makeQuery(id+"F20.imprint","IMPRINT",EDGE,{"derivedFrom":sQuery(id+"F20.wireOp",EDGE,"E620.bottom")}),1.0]])]});
            extrude(context, id + "F21", {"entities" : qUnion([Q0, Q1, Q2, Q3, Q4, Q5]), "depth" : 4 * mm});
        }
        {
            var Q0;
            {var subQ12=sQuery(id+"F20.wireOp",EDGE,"274de717-3da0-4c64-9ed4-fe21729b6c2f");Q0=makeQuery(id+"F20.imprint","IMPRINT",FACE,{"disambiguationData":[TD([[makeQuery(id+"F20.imprint","IMPRINT",EDGE,{"derivedFrom":subQ12}),-1.0]])]});}
            var Q1;
            {var subQ8=sQuery(id+"F20.wireOp",EDGE,"1e5e7644-ac6b-445a-a06a-048c4de03991");Q1=makeQuery(id+"F20.imprint","IMPRINT",FACE,{"disambiguationData":[TD([[makeQuery(id+"F20.imprint","IMPRINT",EDGE,{"derivedFrom":subQ8}),-1.0]])]});}
            var Q2;
            Q2=makeQuery(id+"F20.imprint","IMPRINT",FACE,{"disambiguationData":[TD([[makeQuery(id+"F20.imprint","IMPRINT",EDGE,{"derivedFrom":sQuery(id+"F20.wireOp",EDGE,"E495.MirrorCS")}),-1.0]])]});
            extrude(context, id + "F22", {"entities" : qUnion([Q0, Q1, Q2]), "operationType" : NewBodyOperationType.ADD, "depth" : 4 * mm});
        }
        {
            var Q0;
            Q0=makeQuery(id+"F20.imprint","IMPRINT",FACE,{"disambiguationData":[TD([[makeQuery(id+"F20.imprint","IMPRINT",EDGE,{"derivedFrom":sQuery(id+"F20.wireOp",EDGE,"E557.left")}),1.0]])]});
            extrude(context, id + "F23", {"entities" : qUnion([Q0]), "depth" : 4 * mm});
        }
        {
            var Q0;
            Q0=qCreatedBy(makeId("Top.planeOp"),FACE);
            var sketch = newSketch(context, id + "F24", { "sketchPlane" : qUnion([Q0])});
            skLineSegment(sketch, "E648.bottom", {"start": v(-974.65, 66.8) * mm, "end": v(-646.65, 66.8) * mm});
            skLineSegment(sketch, "E648.top", {"start": v(-974.65, -273.2) * mm, "end": v(-646.65, -273.2) * mm});
            skLineSegment(sketch, "E648.left", {"start": v(-974.65, 66.8) * mm, "end": v(-974.65, -273.2) * mm});
            skLineSegment(sketch, "E648.right", {"start": v(-646.65, 66.8) * mm, "end": v(-646.65, -273.2) * mm});
            skPoint(sketch, "E649", {"position": v(-646.65, -253.2) * mm});
            skLineSegment(sketch, "E650", {"start": v(-646.65, -253.2) * mm, "end": v(-974.65, -253.2) * mm, "construction": true});
            skPoint(sketch, "E651", {"position": v(-666.65, -273.2) * mm});
            skLineSegment(sketch, "E652", {"start": v(-666.65, -273.2) * mm, "end": v(-666.65, 66.8) * mm, "construction": true});
            skLineSegment(sketch, "E653.MirrorCS", {"start": v(-954.65, -273.2) * mm, "end": v(-954.65, 56.8) * mm, "construction": true});
            skLineSegment(sketch, "E654.MirrorCS", {"start": v(-646.65, 46.8) * mm, "end": v(-974.65, 46.8) * mm, "construction": true});
            skLineSegment(sketch, "E655", {"start": v(-974.65, -253.2) * mm, "end": v(-954.65, -253.2) * mm});
            skLineSegment(sketch, "E656", {"start": v(-954.65, -253.2) * mm, "end": v(-954.65, 46.8) * mm});
            skLineSegment(sketch, "E657", {"start": v(-954.65, 46.8) * mm, "end": v(-974.65, 46.8) * mm});
            skLineSegment(sketch, "E658", {"start": v(-646.65, -253.2) * mm, "end": v(-666.65, -253.2) * mm});
            skLineSegment(sketch, "E659", {"start": v(-666.65, -253.2) * mm, "end": v(-666.65, 46.8) * mm});
            skLineSegment(sketch, "E660", {"start": v(-666.65, 46.8) * mm, "end": v(-646.65, 46.8) * mm});
            skLineSegment(sketch, "E661.bottom", {"start": v(-1090.94, -273.2) * mm, "end": v(-1150.94, -273.2) * mm});
            skLineSegment(sketch, "E661.top", {"start": v(-1090.94, 66.8) * mm, "end": v(-1150.94, 66.8) * mm});
            skLineSegment(sketch, "E661.left", {"start": v(-1090.94, -273.2) * mm, "end": v(-1090.94, 66.8) * mm});
            skLineSegment(sketch, "E661.right", {"start": v(-1150.94, -273.2) * mm, "end": v(-1150.94, 66.8) * mm});
            skSolve(sketch);
        }
        {
            var Q0;
            Q0=makeQuery(id+"F24.imprint","IMPRINT",FACE,{"disambiguationData":[TD([[makeQuery(id+"F24.imprint","IMPRINT",EDGE,{"derivedFrom":sQuery(id+"F24.wireOp",EDGE,"E648.bottom")}),-1.0]])]});
            var Q1;
            {var subQ0=sQuery(id+"F24.wireOp",EDGE,"E655");Q1=makeQuery(id+"F24.imprint","IMPRINT",FACE,{"disambiguationData":[TD([[makeQuery(id+"F24.imprint","IMPRINT",EDGE,{"derivedFrom":subQ0}),1.0]])]});}
            var Q2;
            {var subQ0=sQuery(id+"F24.wireOp",EDGE,"E658");Q2=makeQuery(id+"F24.imprint","IMPRINT",FACE,{"disambiguationData":[TD([[makeQuery(id+"F24.imprint","IMPRINT",EDGE,{"derivedFrom":subQ0}),-1.0]])]});}
            extrude(context, id + "F25", {"entities" : qUnion([Q0, Q1, Q2]), "depth" : 18 * mm});
        }
        {
            var Q0;
            Q0=makeQuery(id+"F24.imprint","IMPRINT",FACE,{"disambiguationData":[TD([[makeQuery(id+"F24.imprint","IMPRINT",EDGE,{"derivedFrom":sQuery(id+"F24.wireOp",EDGE,"E661.bottom")}),-1.0]])]});
            extrude(context, id + "F26", {"entities" : qUnion([Q0]), "depth" : 2 * mm});
        }
        {
            var Q0;
            Q0=makeQuery(id+"F25.opExtrude","SWEPT_FACE",FACE,{"disambiguationData":[OSD([sQuery(id+"F24.wireOp",EDGE,"E648.top")])]});
            var sketch = newSketch(context, id + "F27", { "sketchPlane" : qUnion([Q0])});
            skLineSegment(sketch, "E662", {"start": v(-967.65, 18) * mm, "end": v(-962.65, 18) * mm, "construction": true});
            skLineSegment(sketch, "E663", {"start": v(-810.65, 18) * mm, "end": v(-810.65, 0) * mm, "construction": true});
            skArc(sketch, "E664", {"start": v(-967.65, 9) * mm, "mid": v(-962.65, 4) * mm, "end": v(-957.65, 9) * mm});
            skPoint(sketch, "E664.centerSnap0", {"position": v(-974.65, 9) * mm});
            skLineSegment(sketch, "E665", {"start": v(-967.65, 9) * mm, "end": v(-967.65, 18) * mm});
            skLineSegment(sketch, "E666", {"start": v(-957.65, 9) * mm, "end": v(-957.65, 18) * mm});
            skLineSegment(sketch, "E667", {"start": v(-957.65, 18) * mm, "end": v(-967.65, 18) * mm});
            skLineSegment(sketch, "E668.MirrorCS", {"start": v(-663.65, 9) * mm, "end": v(-663.65, 18) * mm});
            skLineSegment(sketch, "E669.MirrorCS", {"start": v(-663.65, 18) * mm, "end": v(-653.65, 18) * mm});
            skLineSegment(sketch, "E670.MirrorCS", {"start": v(-653.65, 9) * mm, "end": v(-653.65, 18) * mm});
            skArc(sketch, "E671.MirrorCS", {"start": v(-653.65, 9) * mm, "mid": v(-658.65, 4) * mm, "end": v(-663.65, 9) * mm});
            skSolve(sketch);
        }
        {
            var Q0;
            Q0=makeQuery(id+"F27.imprint","IMPRINT",FACE,{"disambiguationData":[TD([[makeQuery(id+"F27.imprint","IMPRINT",EDGE,{"derivedFrom":sQuery(id+"F27.wireOp",EDGE,"E664")}),1.0]])]});
            var Q1;
            Q1=makeQuery(id+"F27.imprint","IMPRINT",FACE,{"disambiguationData":[TD([[makeQuery(id+"F27.imprint","IMPRINT",EDGE,{"derivedFrom":sQuery(id+"F27.wireOp",EDGE,"E668.MirrorCS")}),-1.0]])]});
            var Q2;
            Q2=makeQuery(id+"F25.opExtrude","SWEPT_BODY",BODY,{"disambiguationData":[OSD([sQuery(id+"F24.wireOp",EDGE,"E648.bottom"),sQuery(id+"F24.wireOp",EDGE,"E648.top"),sQuery(id+"F24.wireOp",EDGE,"E648.left"),sQuery(id+"F24.wireOp",EDGE,"E648.right")])]});
            extrude(context, id + "F28", {"entities" : qUnion([Q0, Q1]), "operationType" : NewBodyOperationType.REMOVE, "oppositeDirection" : true, "endBoundEntityBody" : qUnion([Q2]), "depth" : 320 * mm, "hasSecondDirection" : true, "secondDirectionOppositeDirection" : true, "secondDirectionDepth" : 20 * mm});
        }
        {
            var Q0;
            Q0=qCreatedBy(makeId("Top.planeOp"),FACE);
            var sketch = newSketch(context, id + "F29", { "sketchPlane" : qUnion([Q0])});
            skLineSegment(sketch, "E672", {"start": v(437.77, -1452.9) * mm, "end": v(433.21, -1452.9) * mm});
            skArc(sketch, "E673", {"start": v(433.41, -1451.7) * mm, "mid": v(433.14, -1451.55) * mm, "end": v(433, -1451.28) * mm});
            skLineSegment(sketch, "E674", {"start": v(431.8, -1451.48) * mm, "end": v(431.8, -1447.15) * mm});
            skLineSegment(sketch, "E675", {"start": v(433.41, -1451.7) * mm, "end": v(436.41, -1451.7) * mm});
            skLineSegment(sketch, "E676", {"start": v(438.2, -1451.13) * mm, "end": v(439.26, -1451.13) * mm});
            skLineSegment(sketch, "E677", {"start": v(431.8, -1434.31) * mm, "end": v(431.8, -1438.65) * mm});
            skLineSegment(sketch, "E678", {"start": v(433, -1448.28) * mm, "end": v(433, -1451.28) * mm});
            skLineSegment(sketch, "E679", {"start": v(432.04, -1446.59) * mm, "end": v(433.32, -1445.3) * mm});
            skLineSegment(sketch, "E680", {"start": v(432.04, -1439.2) * mm, "end": v(433.32, -1440.49) * mm});
            skLineSegment(sketch, "E681", {"start": v(433.66, -1446.5) * mm, "end": v(436.78, -1446.5) * mm});
            skArc(sketch, "E682", {"start": v(433, -1448.28) * mm, "mid": v(433.1, -1447.9) * mm, "end": v(433.42, -1447.7) * mm});
            skLineSegment(sketch, "E683", {"start": v(436.42, -1447.7) * mm, "end": v(433.42, -1447.7) * mm});
            skLineSegment(sketch, "E684", {"start": v(445.85, -1452.9) * mm, "end": v(450.4, -1452.9) * mm});
            skArc(sketch, "E685", {"start": v(450.4, -1452.9) * mm, "mid": v(451.38, -1452.45) * mm, "end": v(451.8, -1451.48) * mm});
            skLineSegment(sketch, "E686", {"start": v(439.44, -1451.56) * mm, "end": v(438.33, -1452.66) * mm});
            skLineSegment(sketch, "E687", {"start": v(451.8, -1451.48) * mm, "end": v(451.8, -1447.15) * mm});
            skLineSegment(sketch, "E688", {"start": v(438.2, -1447.93) * mm, "end": v(438.2, -1451.13) * mm});
            skLineSegment(sketch, "E689", {"start": v(446.84, -1439.3) * mm, "end": v(445.2, -1440.93) * mm});
            skArc(sketch, "E690", {"start": v(450.2, -1451.7) * mm, "mid": v(450.48, -1451.55) * mm, "end": v(450.6, -1451.28) * mm});
            skLineSegment(sketch, "E691", {"start": v(437, -1451.28) * mm, "end": v(437, -1448.28) * mm});
            skLineSegment(sketch, "E692", {"start": v(450.2, -1451.7) * mm, "end": v(447.2, -1451.7) * mm});
            skArc(sketch, "E693", {"start": v(446.6, -1451.28) * mm, "mid": v(446.82, -1451.62) * mm, "end": v(447.2, -1451.7) * mm});
            skLineSegment(sketch, "E694", {"start": v(446.6, -1451.28) * mm, "end": v(446.6, -1448.28) * mm});
            skLineSegment(sketch, "E695", {"start": v(451.58, -1439.2) * mm, "end": v(450.3, -1440.49) * mm});
            skLineSegment(sketch, "E696", {"start": v(451.8, -1434.31) * mm, "end": v(451.8, -1438.65) * mm});
            skLineSegment(sketch, "E697", {"start": v(439.44, -1434.23) * mm, "end": v(438.33, -1433.13) * mm});
            skLineSegment(sketch, "E698", {"start": v(445.85, -1432.9) * mm, "end": v(450.4, -1432.9) * mm});
            skArc(sketch, "E699", {"start": v(450.3, -1445.3) * mm, "mid": v(450.08, -1445.26) * mm, "end": v(449.95, -1445.44) * mm});
            skLineSegment(sketch, "E700", {"start": v(437.77, -1432.9) * mm, "end": v(433.21, -1432.9) * mm});
            skLineSegment(sketch, "E701", {"start": v(449.95, -1445.44) * mm, "end": v(449.95, -1446.5) * mm});
            skArc(sketch, "E702", {"start": v(433.21, -1432.9) * mm, "mid": v(432.24, -1433.34) * mm, "end": v(431.8, -1434.31) * mm});
            skLineSegment(sketch, "E703", {"start": v(449.95, -1446.5) * mm, "end": v(446.84, -1446.5) * mm});
            skLineSegment(sketch, "E704", {"start": v(433.41, -1434.1) * mm, "end": v(436.41, -1434.1) * mm});
            skLineSegment(sketch, "E705", {"start": v(450.2, -1434.1) * mm, "end": v(447.2, -1434.1) * mm});
            skLineSegment(sketch, "E706", {"start": v(445.4, -1434.66) * mm, "end": v(444.36, -1434.66) * mm});
            skLineSegment(sketch, "E707", {"start": v(445.2, -1444.86) * mm, "end": v(445.2, -1443.28) * mm});
            skLineSegment(sketch, "E708", {"start": v(442.1, -1446.33) * mm, "end": v(443.82, -1446.33) * mm});
            skLineSegment(sketch, "E709", {"start": v(445.4, -1437.86) * mm, "end": v(445.4, -1434.66) * mm});
            skLineSegment(sketch, "E710", {"start": v(443.82, -1446.33) * mm, "end": v(445.4, -1447.93) * mm});
            skLineSegment(sketch, "E711", {"start": v(437, -1434.51) * mm, "end": v(437, -1437.51) * mm});
            skLineSegment(sketch, "E712", {"start": v(433.66, -1439.3) * mm, "end": v(436.78, -1439.3) * mm});
            skLineSegment(sketch, "E713", {"start": v(438.4, -1440.93) * mm, "end": v(438.4, -1442.51) * mm});
            skLineSegment(sketch, "E714", {"start": v(436.78, -1446.5) * mm, "end": v(438.4, -1444.86) * mm});
            skLineSegment(sketch, "E715", {"start": v(445.4, -1447.93) * mm, "end": v(445.4, -1451.13) * mm});
            skLineSegment(sketch, "E716", {"start": v(443.82, -1439.46) * mm, "end": v(445.4, -1437.86) * mm});
            skLineSegment(sketch, "E717", {"start": v(442.1, -1439.46) * mm, "end": v(443.82, -1439.46) * mm});
            skLineSegment(sketch, "E718", {"start": v(449.95, -1439.3) * mm, "end": v(446.84, -1439.3) * mm});
            skArc(sketch, "E719", {"start": v(445.29, -1452.66) * mm, "mid": v(445.55, -1452.83) * mm, "end": v(445.85, -1452.9) * mm});
            skLineSegment(sketch, "E720", {"start": v(449.95, -1440.36) * mm, "end": v(449.95, -1439.3) * mm});
            skCircle(sketch, "E721", {"center": v(441.8, -1442.9) * mm, "radius": 2.1 * mm});
            skLineSegment(sketch, "E722", {"start": v(450.6, -1437.51) * mm, "end": v(450.6, -1434.51) * mm});
            skLineSegment(sketch, "E723", {"start": v(438.2, -1434.66) * mm, "end": v(439.26, -1434.66) * mm});
            skLineSegment(sketch, "E724", {"start": v(451.58, -1446.59) * mm, "end": v(450.3, -1445.3) * mm});
            skLineSegment(sketch, "E725", {"start": v(436.42, -1438.1) * mm, "end": v(433.42, -1438.1) * mm});
            skLineSegment(sketch, "E726", {"start": v(439.8, -1446.33) * mm, "end": v(438.2, -1447.93) * mm});
            skLineSegment(sketch, "E727", {"start": v(441.5, -1446.33) * mm, "end": v(439.8, -1446.33) * mm});
            skLineSegment(sketch, "E728", {"start": v(433, -1437.51) * mm, "end": v(433, -1434.51) * mm});
            skLineSegment(sketch, "E729", {"start": v(446.6, -1434.51) * mm, "end": v(446.6, -1437.51) * mm});
            skLineSegment(sketch, "E730", {"start": v(444.18, -1434.23) * mm, "end": v(445.29, -1433.13) * mm});
            skLineSegment(sketch, "E731", {"start": v(441.8, -1446.07) * mm, "end": v(441.5, -1446.33) * mm});
            skArc(sketch, "E732", {"start": v(444.36, -1434.66) * mm, "mid": v(444.13, -1434.5) * mm, "end": v(444.18, -1434.23) * mm});
            skLineSegment(sketch, "E733", {"start": v(446.84, -1446.5) * mm, "end": v(445.2, -1444.86) * mm});
            skLineSegment(sketch, "E734", {"start": v(438.4, -1444.86) * mm, "end": v(438.4, -1443.28) * mm});
            skLineSegment(sketch, "E735", {"start": v(447.2, -1447.7) * mm, "end": v(450.2, -1447.7) * mm});
            skLineSegment(sketch, "E736", {"start": v(445.4, -1451.13) * mm, "end": v(444.36, -1451.13) * mm});
            skLineSegment(sketch, "E737", {"start": v(450.6, -1448.28) * mm, "end": v(450.6, -1451.28) * mm});
            skLineSegment(sketch, "E738", {"start": v(438.2, -1437.86) * mm, "end": v(438.2, -1434.66) * mm});
            skLineSegment(sketch, "E739", {"start": v(447.2, -1438.1) * mm, "end": v(450.2, -1438.1) * mm});
            skLineSegment(sketch, "E740", {"start": v(436.78, -1439.3) * mm, "end": v(438.4, -1440.93) * mm});
            skLineSegment(sketch, "E741", {"start": v(439.8, -1439.46) * mm, "end": v(438.2, -1437.86) * mm});
            skArc(sketch, "E742", {"start": v(450.6, -1437.51) * mm, "mid": v(450.53, -1437.9) * mm, "end": v(450.2, -1438.1) * mm});
            skLineSegment(sketch, "E743", {"start": v(441.5, -1439.46) * mm, "end": v(439.8, -1439.46) * mm});
            skArc(sketch, "E744", {"start": v(451.8, -1438.65) * mm, "mid": v(451.75, -1438.95) * mm, "end": v(451.58, -1439.2) * mm});
            skArc(sketch, "E745", {"start": v(433.21, -1452.9) * mm, "mid": v(432.24, -1452.45) * mm, "end": v(431.8, -1451.48) * mm});
            skArc(sketch, "E746", {"start": v(450.4, -1432.9) * mm, "mid": v(451.38, -1433.34) * mm, "end": v(451.8, -1434.31) * mm});
            skLineSegment(sketch, "E747", {"start": v(445.2, -1442.51) * mm, "end": v(444.83, -1442.9) * mm});
            skArc(sketch, "E748", {"start": v(450.6, -1448.28) * mm, "mid": v(450.53, -1447.9) * mm, "end": v(450.2, -1447.7) * mm});
            skLineSegment(sketch, "E749", {"start": v(445.2, -1440.93) * mm, "end": v(445.2, -1442.51) * mm});
            skArc(sketch, "E750", {"start": v(436.42, -1447.7) * mm, "mid": v(436.87, -1447.83) * mm, "end": v(437, -1448.28) * mm});
            skLineSegment(sketch, "E751", {"start": v(441.8, -1439.72) * mm, "end": v(442.1, -1439.46) * mm});
            skLineSegment(sketch, "E752", {"start": v(441.8, -1439.72) * mm, "end": v(441.5, -1439.46) * mm});
            skLineSegment(sketch, "E753", {"start": v(444.18, -1451.56) * mm, "end": v(445.29, -1452.66) * mm});
            skArc(sketch, "E754", {"start": v(437, -1451.28) * mm, "mid": v(436.8, -1451.62) * mm, "end": v(436.41, -1451.7) * mm});
            skArc(sketch, "E755", {"start": v(438.33, -1452.66) * mm, "mid": v(438.07, -1452.83) * mm, "end": v(437.77, -1452.9) * mm});
            skArc(sketch, "E756", {"start": v(439.26, -1451.13) * mm, "mid": v(439.5, -1451.29) * mm, "end": v(439.44, -1451.56) * mm});
            skArc(sketch, "E757", {"start": v(451.8, -1447.15) * mm, "mid": v(451.75, -1446.84) * mm, "end": v(451.58, -1446.59) * mm});
            skArc(sketch, "E758", {"start": v(436.42, -1438.1) * mm, "mid": v(436.87, -1437.96) * mm, "end": v(437, -1437.51) * mm});
            skArc(sketch, "E759", {"start": v(438.33, -1433.13) * mm, "mid": v(438.07, -1432.96) * mm, "end": v(437.77, -1432.9) * mm});
            skArc(sketch, "E760", {"start": v(433, -1437.51) * mm, "mid": v(433.1, -1437.9) * mm, "end": v(433.42, -1438.1) * mm});
            skArc(sketch, "E761", {"start": v(447.2, -1438.1) * mm, "mid": v(446.75, -1437.96) * mm, "end": v(446.6, -1437.51) * mm});
            skArc(sketch, "E762", {"start": v(445.29, -1433.13) * mm, "mid": v(445.55, -1432.96) * mm, "end": v(445.85, -1432.9) * mm});
            skArc(sketch, "E763", {"start": v(433.41, -1434.1) * mm, "mid": v(433.14, -1434.24) * mm, "end": v(433, -1434.51) * mm});
            skArc(sketch, "E764", {"start": v(446.6, -1434.51) * mm, "mid": v(446.82, -1434.18) * mm, "end": v(447.2, -1434.1) * mm});
            skLineSegment(sketch, "E765", {"start": v(441.8, -1446.07) * mm, "end": v(442.1, -1446.33) * mm});
            skArc(sketch, "E766", {"start": v(431.8, -1438.65) * mm, "mid": v(431.87, -1438.95) * mm, "end": v(432.04, -1439.2) * mm});
            skArc(sketch, "E767", {"start": v(437, -1434.51) * mm, "mid": v(436.8, -1434.18) * mm, "end": v(436.41, -1434.1) * mm});
            skLineSegment(sketch, "E768", {"start": v(445.2, -1443.28) * mm, "end": v(444.83, -1442.9) * mm});
            skArc(sketch, "E769", {"start": v(447.2, -1447.7) * mm, "mid": v(446.75, -1447.83) * mm, "end": v(446.6, -1448.28) * mm});
            skArc(sketch, "E770", {"start": v(431.8, -1447.15) * mm, "mid": v(431.87, -1446.84) * mm, "end": v(432.04, -1446.59) * mm});
            skLineSegment(sketch, "E771", {"start": v(433.66, -1440.36) * mm, "end": v(433.66, -1439.3) * mm});
            skLineSegment(sketch, "E772", {"start": v(438.4, -1442.51) * mm, "end": v(438.8, -1442.9) * mm});
            skLineSegment(sketch, "E773", {"start": v(438.4, -1443.28) * mm, "end": v(438.8, -1442.9) * mm});
            skLineSegment(sketch, "E774", {"start": v(433.66, -1445.44) * mm, "end": v(433.66, -1446.5) * mm});
            skArc(sketch, "E775", {"start": v(433.32, -1445.3) * mm, "mid": v(433.54, -1445.26) * mm, "end": v(433.66, -1445.44) * mm});
            skArc(sketch, "E776", {"start": v(444.36, -1451.13) * mm, "mid": v(444.13, -1451.29) * mm, "end": v(444.18, -1451.56) * mm});
            skArc(sketch, "E777", {"start": v(450.3, -1440.49) * mm, "mid": v(450.08, -1440.53) * mm, "end": v(449.95, -1440.36) * mm});
            skArc(sketch, "E778", {"start": v(439.26, -1434.66) * mm, "mid": v(439.5, -1434.5) * mm, "end": v(439.44, -1434.23) * mm});
            skArc(sketch, "E779", {"start": v(450.2, -1434.1) * mm, "mid": v(450.48, -1434.24) * mm, "end": v(450.6, -1434.51) * mm});
            skArc(sketch, "E780", {"start": v(433.32, -1440.49) * mm, "mid": v(433.54, -1440.53) * mm, "end": v(433.66, -1440.36) * mm});
            skLineSegment(sketch, "E781", {"start": v(469.37, -1445.8) * mm, "end": v(464.81, -1445.8) * mm});
            skArc(sketch, "E782", {"start": v(465.01, -1444.6) * mm, "mid": v(464.74, -1444.45) * mm, "end": v(464.6, -1444.17) * mm});
            skLineSegment(sketch, "E783", {"start": v(463.4, -1444.37) * mm, "end": v(463.4, -1440.04) * mm});
            skLineSegment(sketch, "E784", {"start": v(465.01, -1444.6) * mm, "end": v(468.01, -1444.6) * mm});
            skLineSegment(sketch, "E785", {"start": v(469.8, -1444.03) * mm, "end": v(470.86, -1444.03) * mm});
            skLineSegment(sketch, "E786", {"start": v(463.4, -1427.21) * mm, "end": v(463.4, -1431.54) * mm});
            skLineSegment(sketch, "E787", {"start": v(464.6, -1441.17) * mm, "end": v(464.6, -1444.17) * mm});
            skLineSegment(sketch, "E788", {"start": v(463.64, -1439.48) * mm, "end": v(464.92, -1438.2) * mm});
            skLineSegment(sketch, "E789", {"start": v(463.64, -1432.1) * mm, "end": v(464.92, -1433.38) * mm});
            skLineSegment(sketch, "E790", {"start": v(465.26, -1439.4) * mm, "end": v(468.38, -1439.4) * mm});
            skArc(sketch, "E791", {"start": v(464.6, -1441.17) * mm, "mid": v(464.7, -1440.8) * mm, "end": v(465.02, -1440.6) * mm});
            skLineSegment(sketch, "E792", {"start": v(468.02, -1440.6) * mm, "end": v(465.02, -1440.6) * mm});
            skLineSegment(sketch, "E793", {"start": v(477.45, -1445.8) * mm, "end": v(482, -1445.8) * mm});
            skArc(sketch, "E794", {"start": v(482, -1445.8) * mm, "mid": v(482.98, -1445.35) * mm, "end": v(483.4, -1444.37) * mm});
            skLineSegment(sketch, "E795", {"start": v(471.04, -1444.45) * mm, "end": v(469.93, -1445.56) * mm});
            skLineSegment(sketch, "E796", {"start": v(483.4, -1444.37) * mm, "end": v(483.4, -1440.04) * mm});
            skLineSegment(sketch, "E797", {"start": v(469.8, -1440.83) * mm, "end": v(469.8, -1444.03) * mm});
            skLineSegment(sketch, "E798", {"start": v(478.44, -1432.2) * mm, "end": v(476.8, -1433.83) * mm});
            skArc(sketch, "E799", {"start": v(481.8, -1444.6) * mm, "mid": v(482.08, -1444.45) * mm, "end": v(482.2, -1444.17) * mm});
            skLineSegment(sketch, "E800", {"start": v(468.6, -1444.17) * mm, "end": v(468.6, -1441.17) * mm});
            skLineSegment(sketch, "E801", {"start": v(481.8, -1444.6) * mm, "end": v(478.8, -1444.6) * mm});
            skArc(sketch, "E802", {"start": v(478.2, -1444.17) * mm, "mid": v(478.42, -1444.51) * mm, "end": v(478.8, -1444.6) * mm});
            skLineSegment(sketch, "E803", {"start": v(478.2, -1444.17) * mm, "end": v(478.2, -1441.17) * mm});
            skLineSegment(sketch, "E804", {"start": v(483.18, -1432.1) * mm, "end": v(481.9, -1433.38) * mm});
            skLineSegment(sketch, "E805", {"start": v(483.4, -1427.21) * mm, "end": v(483.4, -1431.54) * mm});
            skLineSegment(sketch, "E806", {"start": v(471.04, -1427.13) * mm, "end": v(469.93, -1426.03) * mm});
            skLineSegment(sketch, "E807", {"start": v(477.45, -1425.8) * mm, "end": v(482, -1425.8) * mm});
            skArc(sketch, "E808", {"start": v(481.9, -1438.2) * mm, "mid": v(481.68, -1438.16) * mm, "end": v(481.55, -1438.33) * mm});
            skLineSegment(sketch, "E809", {"start": v(469.37, -1425.8) * mm, "end": v(464.81, -1425.8) * mm});
            skLineSegment(sketch, "E810", {"start": v(481.55, -1438.33) * mm, "end": v(481.55, -1439.4) * mm});
            skArc(sketch, "E811", {"start": v(464.81, -1425.8) * mm, "mid": v(463.84, -1426.23) * mm, "end": v(463.4, -1427.21) * mm});
            skLineSegment(sketch, "E812", {"start": v(481.55, -1439.4) * mm, "end": v(478.44, -1439.4) * mm});
            skLineSegment(sketch, "E813", {"start": v(465.01, -1427) * mm, "end": v(468.01, -1427) * mm});
            skLineSegment(sketch, "E814", {"start": v(481.8, -1427) * mm, "end": v(478.8, -1427) * mm});
            skLineSegment(sketch, "E815", {"start": v(477, -1427.56) * mm, "end": v(475.96, -1427.56) * mm});
            skLineSegment(sketch, "E816", {"start": v(476.8, -1437.76) * mm, "end": v(476.8, -1436.17) * mm});
            skLineSegment(sketch, "E817", {"start": v(473.7, -1439.23) * mm, "end": v(475.41, -1439.23) * mm});
            skLineSegment(sketch, "E818", {"start": v(477, -1430.76) * mm, "end": v(477, -1427.56) * mm});
            skLineSegment(sketch, "E819", {"start": v(475.41, -1439.23) * mm, "end": v(477, -1440.83) * mm});
            skLineSegment(sketch, "E820", {"start": v(468.6, -1427.41) * mm, "end": v(468.6, -1430.41) * mm});
            skLineSegment(sketch, "E821", {"start": v(465.26, -1432.2) * mm, "end": v(468.38, -1432.2) * mm});
            skLineSegment(sketch, "E822", {"start": v(470, -1433.83) * mm, "end": v(470, -1435.41) * mm});
            skLineSegment(sketch, "E823", {"start": v(468.38, -1439.4) * mm, "end": v(470, -1437.76) * mm});
            skLineSegment(sketch, "E824", {"start": v(477, -1440.83) * mm, "end": v(477, -1444.03) * mm});
            skLineSegment(sketch, "E825", {"start": v(475.41, -1432.36) * mm, "end": v(477, -1430.76) * mm});
            skLineSegment(sketch, "E826", {"start": v(473.7, -1432.36) * mm, "end": v(475.41, -1432.36) * mm});
            skLineSegment(sketch, "E827", {"start": v(481.55, -1432.2) * mm, "end": v(478.44, -1432.2) * mm});
            skArc(sketch, "E828", {"start": v(476.89, -1445.56) * mm, "mid": v(477.15, -1445.73) * mm, "end": v(477.45, -1445.8) * mm});
            skLineSegment(sketch, "E829", {"start": v(481.55, -1433.25) * mm, "end": v(481.55, -1432.2) * mm});
            skCircle(sketch, "E830", {"center": v(473.4, -1435.8) * mm, "radius": 2.1 * mm});
            skLineSegment(sketch, "E831", {"start": v(482.2, -1430.41) * mm, "end": v(482.2, -1427.41) * mm});
            skLineSegment(sketch, "E832", {"start": v(469.8, -1427.56) * mm, "end": v(470.86, -1427.56) * mm});
            skLineSegment(sketch, "E833", {"start": v(483.18, -1439.48) * mm, "end": v(481.9, -1438.2) * mm});
            skLineSegment(sketch, "E834", {"start": v(468.02, -1431) * mm, "end": v(465.02, -1431) * mm});
            skLineSegment(sketch, "E835", {"start": v(471.4, -1439.23) * mm, "end": v(469.8, -1440.83) * mm});
            skLineSegment(sketch, "E836", {"start": v(473.1, -1439.23) * mm, "end": v(471.4, -1439.23) * mm});
            skLineSegment(sketch, "E837", {"start": v(464.6, -1430.41) * mm, "end": v(464.6, -1427.41) * mm});
            skLineSegment(sketch, "E838", {"start": v(478.2, -1427.41) * mm, "end": v(478.2, -1430.41) * mm});
            skLineSegment(sketch, "E839", {"start": v(475.78, -1427.13) * mm, "end": v(476.89, -1426.03) * mm});
            skLineSegment(sketch, "E840", {"start": v(473.4, -1438.97) * mm, "end": v(473.1, -1439.23) * mm});
            skArc(sketch, "E841", {"start": v(475.96, -1427.56) * mm, "mid": v(475.73, -1427.4) * mm, "end": v(475.78, -1427.13) * mm});
            skLineSegment(sketch, "E842", {"start": v(478.44, -1439.4) * mm, "end": v(476.8, -1437.76) * mm});
            skLineSegment(sketch, "E843", {"start": v(470, -1437.76) * mm, "end": v(470, -1436.17) * mm});
            skLineSegment(sketch, "E844", {"start": v(478.8, -1440.6) * mm, "end": v(481.8, -1440.6) * mm});
            skLineSegment(sketch, "E845", {"start": v(477, -1444.03) * mm, "end": v(475.96, -1444.03) * mm});
            skLineSegment(sketch, "E846", {"start": v(482.2, -1441.17) * mm, "end": v(482.2, -1444.17) * mm});
            skLineSegment(sketch, "E847", {"start": v(469.8, -1430.76) * mm, "end": v(469.8, -1427.56) * mm});
            skLineSegment(sketch, "E848", {"start": v(478.8, -1431) * mm, "end": v(481.8, -1431) * mm});
            skLineSegment(sketch, "E849", {"start": v(468.38, -1432.2) * mm, "end": v(470, -1433.83) * mm});
            skLineSegment(sketch, "E850", {"start": v(471.4, -1432.36) * mm, "end": v(469.8, -1430.76) * mm});
            skArc(sketch, "E851", {"start": v(482.2, -1430.41) * mm, "mid": v(482.13, -1430.79) * mm, "end": v(481.8, -1431) * mm});
            skLineSegment(sketch, "E852", {"start": v(473.1, -1432.36) * mm, "end": v(471.4, -1432.36) * mm});
            skArc(sketch, "E853", {"start": v(483.4, -1431.54) * mm, "mid": v(483.35, -1431.84) * mm, "end": v(483.18, -1432.1) * mm});
            skArc(sketch, "E854", {"start": v(464.81, -1445.8) * mm, "mid": v(463.84, -1445.35) * mm, "end": v(463.4, -1444.37) * mm});
            skArc(sketch, "E855", {"start": v(482, -1425.8) * mm, "mid": v(482.98, -1426.23) * mm, "end": v(483.4, -1427.21) * mm});
            skLineSegment(sketch, "E856", {"start": v(476.8, -1435.41) * mm, "end": v(476.43, -1435.8) * mm});
            skArc(sketch, "E857", {"start": v(482.2, -1441.17) * mm, "mid": v(482.13, -1440.8) * mm, "end": v(481.8, -1440.6) * mm});
            skLineSegment(sketch, "E858", {"start": v(476.8, -1433.83) * mm, "end": v(476.8, -1435.41) * mm});
            skArc(sketch, "E859", {"start": v(468.02, -1440.6) * mm, "mid": v(468.47, -1440.73) * mm, "end": v(468.6, -1441.17) * mm});
            skLineSegment(sketch, "E860", {"start": v(473.4, -1432.62) * mm, "end": v(473.7, -1432.36) * mm});
            skLineSegment(sketch, "E861", {"start": v(473.4, -1432.62) * mm, "end": v(473.1, -1432.36) * mm});
            skLineSegment(sketch, "E862", {"start": v(475.78, -1444.45) * mm, "end": v(476.89, -1445.56) * mm});
            skArc(sketch, "E863", {"start": v(468.6, -1444.17) * mm, "mid": v(468.4, -1444.51) * mm, "end": v(468.01, -1444.6) * mm});
            skArc(sketch, "E864", {"start": v(469.93, -1445.56) * mm, "mid": v(469.67, -1445.73) * mm, "end": v(469.37, -1445.8) * mm});
            skArc(sketch, "E865", {"start": v(470.86, -1444.03) * mm, "mid": v(471.1, -1444.18) * mm, "end": v(471.04, -1444.45) * mm});
            skArc(sketch, "E866", {"start": v(483.4, -1440.04) * mm, "mid": v(483.35, -1439.74) * mm, "end": v(483.18, -1439.48) * mm});
            skArc(sketch, "E867", {"start": v(468.02, -1431) * mm, "mid": v(468.47, -1430.86) * mm, "end": v(468.6, -1430.41) * mm});
            skArc(sketch, "E868", {"start": v(469.93, -1426.03) * mm, "mid": v(469.67, -1425.85) * mm, "end": v(469.37, -1425.8) * mm});
            skArc(sketch, "E869", {"start": v(464.6, -1430.41) * mm, "mid": v(464.7, -1430.79) * mm, "end": v(465.02, -1431) * mm});
            skArc(sketch, "E870", {"start": v(478.8, -1431) * mm, "mid": v(478.35, -1430.86) * mm, "end": v(478.2, -1430.41) * mm});
            skArc(sketch, "E871", {"start": v(476.89, -1426.03) * mm, "mid": v(477.15, -1425.85) * mm, "end": v(477.45, -1425.8) * mm});
            skArc(sketch, "E872", {"start": v(465.01, -1427) * mm, "mid": v(464.74, -1427.14) * mm, "end": v(464.6, -1427.41) * mm});
            skArc(sketch, "E873", {"start": v(478.2, -1427.41) * mm, "mid": v(478.42, -1427.07) * mm, "end": v(478.8, -1427) * mm});
            skLineSegment(sketch, "E874", {"start": v(473.4, -1438.97) * mm, "end": v(473.7, -1439.23) * mm});
            skArc(sketch, "E875", {"start": v(463.4, -1431.54) * mm, "mid": v(463.47, -1431.84) * mm, "end": v(463.64, -1432.1) * mm});
            skArc(sketch, "E876", {"start": v(468.6, -1427.41) * mm, "mid": v(468.4, -1427.07) * mm, "end": v(468.01, -1427) * mm});
            skLineSegment(sketch, "E877", {"start": v(476.8, -1436.17) * mm, "end": v(476.43, -1435.8) * mm});
            skArc(sketch, "E878", {"start": v(478.8, -1440.6) * mm, "mid": v(478.35, -1440.73) * mm, "end": v(478.2, -1441.17) * mm});
            skArc(sketch, "E879", {"start": v(463.4, -1440.04) * mm, "mid": v(463.47, -1439.74) * mm, "end": v(463.64, -1439.48) * mm});
            skLineSegment(sketch, "E880", {"start": v(465.26, -1433.25) * mm, "end": v(465.26, -1432.2) * mm});
            skLineSegment(sketch, "E881", {"start": v(470, -1435.41) * mm, "end": v(470.4, -1435.8) * mm});
            skLineSegment(sketch, "E882", {"start": v(470, -1436.17) * mm, "end": v(470.4, -1435.8) * mm});
            skLineSegment(sketch, "E883", {"start": v(465.26, -1438.33) * mm, "end": v(465.26, -1439.4) * mm});
            skArc(sketch, "E884", {"start": v(464.92, -1438.2) * mm, "mid": v(465.14, -1438.16) * mm, "end": v(465.26, -1438.33) * mm});
            skArc(sketch, "E885", {"start": v(475.96, -1444.03) * mm, "mid": v(475.73, -1444.18) * mm, "end": v(475.78, -1444.45) * mm});
            skArc(sketch, "E886", {"start": v(481.9, -1433.38) * mm, "mid": v(481.68, -1433.43) * mm, "end": v(481.55, -1433.25) * mm});
            skArc(sketch, "E887", {"start": v(470.86, -1427.56) * mm, "mid": v(471.1, -1427.4) * mm, "end": v(471.04, -1427.13) * mm});
            skArc(sketch, "E888", {"start": v(481.8, -1427) * mm, "mid": v(482.08, -1427.14) * mm, "end": v(482.2, -1427.41) * mm});
            skArc(sketch, "E889", {"start": v(464.92, -1433.38) * mm, "mid": v(465.14, -1433.43) * mm, "end": v(465.26, -1433.25) * mm});
            skLineSegment(sketch, "E890", {"start": v(503.22, -1456.98) * mm, "end": v(498.66, -1456.98) * mm});
            skArc(sketch, "E891", {"start": v(498.86, -1455.78) * mm, "mid": v(498.6, -1455.64) * mm, "end": v(498.46, -1455.36) * mm});
            skLineSegment(sketch, "E892", {"start": v(497.26, -1455.56) * mm, "end": v(497.26, -1451.23) * mm});
            skLineSegment(sketch, "E893", {"start": v(498.86, -1455.78) * mm, "end": v(501.86, -1455.78) * mm});
            skLineSegment(sketch, "E894", {"start": v(503.66, -1455.22) * mm, "end": v(504.7, -1455.22) * mm});
            skLineSegment(sketch, "E895", {"start": v(497.26, -1438.4) * mm, "end": v(497.26, -1442.73) * mm});
            skLineSegment(sketch, "E896", {"start": v(498.46, -1452.36) * mm, "end": v(498.46, -1455.36) * mm});
            skLineSegment(sketch, "E897", {"start": v(497.49, -1450.67) * mm, "end": v(498.77, -1449.4) * mm});
            skLineSegment(sketch, "E898", {"start": v(497.49, -1443.3) * mm, "end": v(498.77, -1444.57) * mm});
            skLineSegment(sketch, "E899", {"start": v(499.11, -1450.58) * mm, "end": v(502.23, -1450.58) * mm});
            skArc(sketch, "E900", {"start": v(498.46, -1452.36) * mm, "mid": v(498.54, -1451.99) * mm, "end": v(498.87, -1451.78) * mm});
            skLineSegment(sketch, "E901", {"start": v(501.87, -1451.78) * mm, "end": v(498.87, -1451.78) * mm});
            skLineSegment(sketch, "E902", {"start": v(511.3, -1456.98) * mm, "end": v(515.86, -1456.98) * mm});
            skArc(sketch, "E903", {"start": v(515.86, -1456.98) * mm, "mid": v(516.83, -1456.54) * mm, "end": v(517.26, -1455.56) * mm});
            skLineSegment(sketch, "E904", {"start": v(504.89, -1455.64) * mm, "end": v(503.78, -1456.75) * mm});
            skLineSegment(sketch, "E905", {"start": v(517.26, -1455.56) * mm, "end": v(517.26, -1451.23) * mm});
            skLineSegment(sketch, "E906", {"start": v(503.66, -1452.02) * mm, "end": v(503.66, -1455.22) * mm});
            skLineSegment(sketch, "E907", {"start": v(512.29, -1443.38) * mm, "end": v(510.66, -1445.02) * mm});
            skArc(sketch, "E908", {"start": v(515.66, -1455.78) * mm, "mid": v(515.92, -1455.64) * mm, "end": v(516.06, -1455.36) * mm});
            skLineSegment(sketch, "E909", {"start": v(502.46, -1455.36) * mm, "end": v(502.46, -1452.36) * mm});
            skLineSegment(sketch, "E910", {"start": v(515.66, -1455.78) * mm, "end": v(512.66, -1455.78) * mm});
            skArc(sketch, "E911", {"start": v(512.06, -1455.36) * mm, "mid": v(512.27, -1455.7) * mm, "end": v(512.66, -1455.78) * mm});
            skLineSegment(sketch, "E912", {"start": v(512.06, -1455.36) * mm, "end": v(512.06, -1452.36) * mm});
            skLineSegment(sketch, "E913", {"start": v(517.03, -1443.3) * mm, "end": v(515.74, -1444.57) * mm});
            skLineSegment(sketch, "E914", {"start": v(517.26, -1438.4) * mm, "end": v(517.26, -1442.73) * mm});
            skLineSegment(sketch, "E915", {"start": v(504.89, -1438.32) * mm, "end": v(503.78, -1437.22) * mm});
            skLineSegment(sketch, "E916", {"start": v(511.3, -1436.98) * mm, "end": v(515.86, -1436.98) * mm});
            skArc(sketch, "E917", {"start": v(515.74, -1449.4) * mm, "mid": v(515.53, -1449.35) * mm, "end": v(515.4, -1449.52) * mm});
            skLineSegment(sketch, "E918", {"start": v(503.22, -1436.98) * mm, "end": v(498.66, -1436.98) * mm});
            skLineSegment(sketch, "E919", {"start": v(515.4, -1449.52) * mm, "end": v(515.4, -1450.58) * mm});
            skArc(sketch, "E920", {"start": v(498.66, -1436.98) * mm, "mid": v(497.69, -1437.43) * mm, "end": v(497.26, -1438.4) * mm});
            skLineSegment(sketch, "E921", {"start": v(515.4, -1450.58) * mm, "end": v(512.29, -1450.58) * mm});
            skLineSegment(sketch, "E922", {"start": v(498.86, -1438.18) * mm, "end": v(501.86, -1438.18) * mm});
            skLineSegment(sketch, "E923", {"start": v(515.66, -1438.18) * mm, "end": v(512.66, -1438.18) * mm});
            skLineSegment(sketch, "E924", {"start": v(510.86, -1438.75) * mm, "end": v(509.8, -1438.75) * mm});
            skLineSegment(sketch, "E925", {"start": v(510.66, -1448.95) * mm, "end": v(510.66, -1447.36) * mm});
            skLineSegment(sketch, "E926", {"start": v(507.56, -1450.42) * mm, "end": v(509.26, -1450.42) * mm});
            skLineSegment(sketch, "E927", {"start": v(510.86, -1441.95) * mm, "end": v(510.86, -1438.75) * mm});
            skLineSegment(sketch, "E928", {"start": v(509.26, -1450.42) * mm, "end": v(510.86, -1452.02) * mm});
            skLineSegment(sketch, "E929", {"start": v(502.46, -1438.6) * mm, "end": v(502.46, -1441.6) * mm});
            skLineSegment(sketch, "E930", {"start": v(499.11, -1443.38) * mm, "end": v(502.23, -1443.38) * mm});
            skLineSegment(sketch, "E931", {"start": v(503.86, -1445.02) * mm, "end": v(503.86, -1446.6) * mm});
            skLineSegment(sketch, "E932", {"start": v(502.23, -1450.58) * mm, "end": v(503.86, -1448.95) * mm});
            skLineSegment(sketch, "E933", {"start": v(510.86, -1452.02) * mm, "end": v(510.86, -1455.22) * mm});
            skLineSegment(sketch, "E934", {"start": v(509.26, -1443.55) * mm, "end": v(510.86, -1441.95) * mm});
            skLineSegment(sketch, "E935", {"start": v(507.56, -1443.55) * mm, "end": v(509.26, -1443.55) * mm});
            skLineSegment(sketch, "E936", {"start": v(515.4, -1443.38) * mm, "end": v(512.29, -1443.38) * mm});
            skArc(sketch, "E937", {"start": v(510.74, -1456.75) * mm, "mid": v(511, -1456.92) * mm, "end": v(511.3, -1456.98) * mm});
            skLineSegment(sketch, "E938", {"start": v(515.4, -1444.44) * mm, "end": v(515.4, -1443.38) * mm});
            skCircle(sketch, "E939", {"center": v(507.26, -1446.98) * mm, "radius": 2.1 * mm});
            skLineSegment(sketch, "E940", {"start": v(516.06, -1441.6) * mm, "end": v(516.06, -1438.6) * mm});
            skLineSegment(sketch, "E941", {"start": v(503.66, -1438.75) * mm, "end": v(504.7, -1438.75) * mm});
            skLineSegment(sketch, "E942", {"start": v(517.03, -1450.67) * mm, "end": v(515.74, -1449.4) * mm});
            skLineSegment(sketch, "E943", {"start": v(501.87, -1442.18) * mm, "end": v(498.87, -1442.18) * mm});
            skLineSegment(sketch, "E944", {"start": v(505.25, -1450.42) * mm, "end": v(503.66, -1452.02) * mm});
            skLineSegment(sketch, "E945", {"start": v(506.96, -1450.42) * mm, "end": v(505.25, -1450.42) * mm});
            skLineSegment(sketch, "E946", {"start": v(498.46, -1441.6) * mm, "end": v(498.46, -1438.6) * mm});
            skLineSegment(sketch, "E947", {"start": v(512.06, -1438.6) * mm, "end": v(512.06, -1441.6) * mm});
            skLineSegment(sketch, "E948", {"start": v(509.63, -1438.32) * mm, "end": v(510.74, -1437.22) * mm});
            skLineSegment(sketch, "E949", {"start": v(507.26, -1450.16) * mm, "end": v(506.96, -1450.42) * mm});
            skArc(sketch, "E950", {"start": v(509.8, -1438.75) * mm, "mid": v(509.58, -1438.6) * mm, "end": v(509.63, -1438.32) * mm});
            skLineSegment(sketch, "E951", {"start": v(512.29, -1450.58) * mm, "end": v(510.66, -1448.95) * mm});
            skLineSegment(sketch, "E952", {"start": v(503.86, -1448.95) * mm, "end": v(503.86, -1447.36) * mm});
            skLineSegment(sketch, "E953", {"start": v(512.65, -1451.78) * mm, "end": v(515.65, -1451.78) * mm});
            skLineSegment(sketch, "E954", {"start": v(510.86, -1455.22) * mm, "end": v(509.8, -1455.22) * mm});
            skLineSegment(sketch, "E955", {"start": v(516.06, -1452.36) * mm, "end": v(516.06, -1455.36) * mm});
            skLineSegment(sketch, "E956", {"start": v(503.66, -1441.95) * mm, "end": v(503.66, -1438.75) * mm});
            skLineSegment(sketch, "E957", {"start": v(512.65, -1442.18) * mm, "end": v(515.65, -1442.18) * mm});
            skLineSegment(sketch, "E958", {"start": v(502.23, -1443.38) * mm, "end": v(503.86, -1445.02) * mm});
            skLineSegment(sketch, "E959", {"start": v(505.25, -1443.55) * mm, "end": v(503.66, -1441.95) * mm});
            skArc(sketch, "E960", {"start": v(516.06, -1441.6) * mm, "mid": v(515.97, -1441.98) * mm, "end": v(515.65, -1442.18) * mm});
            skLineSegment(sketch, "E961", {"start": v(506.96, -1443.55) * mm, "end": v(505.25, -1443.55) * mm});
            skArc(sketch, "E962", {"start": v(517.26, -1442.73) * mm, "mid": v(517.2, -1443.04) * mm, "end": v(517.03, -1443.3) * mm});
            skArc(sketch, "E963", {"start": v(498.66, -1456.98) * mm, "mid": v(497.69, -1456.54) * mm, "end": v(497.26, -1455.56) * mm});
            skArc(sketch, "E964", {"start": v(515.86, -1436.98) * mm, "mid": v(516.83, -1437.43) * mm, "end": v(517.26, -1438.4) * mm});
            skLineSegment(sketch, "E965", {"start": v(510.66, -1446.6) * mm, "end": v(510.28, -1446.98) * mm});
            skArc(sketch, "E966", {"start": v(516.06, -1452.36) * mm, "mid": v(515.97, -1451.99) * mm, "end": v(515.65, -1451.78) * mm});
            skLineSegment(sketch, "E967", {"start": v(510.66, -1445.02) * mm, "end": v(510.66, -1446.6) * mm});
            skArc(sketch, "E968", {"start": v(501.87, -1451.78) * mm, "mid": v(502.32, -1451.92) * mm, "end": v(502.46, -1452.36) * mm});
            skLineSegment(sketch, "E969", {"start": v(507.26, -1443.8) * mm, "end": v(507.56, -1443.55) * mm});
            skLineSegment(sketch, "E970", {"start": v(507.26, -1443.8) * mm, "end": v(506.96, -1443.55) * mm});
            skLineSegment(sketch, "E971", {"start": v(509.63, -1455.64) * mm, "end": v(510.74, -1456.75) * mm});
            skArc(sketch, "E972", {"start": v(502.46, -1455.36) * mm, "mid": v(502.25, -1455.7) * mm, "end": v(501.86, -1455.78) * mm});
            skArc(sketch, "E973", {"start": v(503.78, -1456.75) * mm, "mid": v(503.52, -1456.92) * mm, "end": v(503.22, -1456.98) * mm});
            skArc(sketch, "E974", {"start": v(504.7, -1455.22) * mm, "mid": v(504.94, -1455.37) * mm, "end": v(504.89, -1455.64) * mm});
            skArc(sketch, "E975", {"start": v(517.26, -1451.23) * mm, "mid": v(517.2, -1450.93) * mm, "end": v(517.03, -1450.67) * mm});
            skArc(sketch, "E976", {"start": v(501.87, -1442.18) * mm, "mid": v(502.32, -1442.05) * mm, "end": v(502.46, -1441.6) * mm});
            skArc(sketch, "E977", {"start": v(503.78, -1437.22) * mm, "mid": v(503.52, -1437.04) * mm, "end": v(503.22, -1436.98) * mm});
            skArc(sketch, "E978", {"start": v(498.46, -1441.6) * mm, "mid": v(498.54, -1441.98) * mm, "end": v(498.87, -1442.18) * mm});
            skArc(sketch, "E979", {"start": v(512.65, -1442.18) * mm, "mid": v(512.2, -1442.05) * mm, "end": v(512.06, -1441.6) * mm});
            skArc(sketch, "E980", {"start": v(510.74, -1437.22) * mm, "mid": v(511, -1437.04) * mm, "end": v(511.3, -1436.98) * mm});
            skArc(sketch, "E981", {"start": v(498.86, -1438.18) * mm, "mid": v(498.6, -1438.33) * mm, "end": v(498.46, -1438.6) * mm});
            skArc(sketch, "E982", {"start": v(512.06, -1438.6) * mm, "mid": v(512.27, -1438.26) * mm, "end": v(512.66, -1438.18) * mm});
            skLineSegment(sketch, "E983", {"start": v(507.26, -1450.16) * mm, "end": v(507.56, -1450.42) * mm});
            skArc(sketch, "E984", {"start": v(497.26, -1442.73) * mm, "mid": v(497.32, -1443.04) * mm, "end": v(497.49, -1443.3) * mm});
            skArc(sketch, "E985", {"start": v(502.46, -1438.6) * mm, "mid": v(502.25, -1438.26) * mm, "end": v(501.86, -1438.18) * mm});
            skLineSegment(sketch, "E986", {"start": v(510.66, -1447.36) * mm, "end": v(510.28, -1446.98) * mm});
            skArc(sketch, "E987", {"start": v(512.65, -1451.78) * mm, "mid": v(512.2, -1451.92) * mm, "end": v(512.06, -1452.36) * mm});
            skArc(sketch, "E988", {"start": v(497.26, -1451.23) * mm, "mid": v(497.32, -1450.93) * mm, "end": v(497.49, -1450.67) * mm});
            skLineSegment(sketch, "E989", {"start": v(499.11, -1444.44) * mm, "end": v(499.11, -1443.38) * mm});
            skLineSegment(sketch, "E990", {"start": v(503.86, -1446.6) * mm, "end": v(504.24, -1446.98) * mm});
            skLineSegment(sketch, "E991", {"start": v(503.86, -1447.36) * mm, "end": v(504.24, -1446.98) * mm});
            skLineSegment(sketch, "E992", {"start": v(499.11, -1449.52) * mm, "end": v(499.11, -1450.58) * mm});
            skArc(sketch, "E993", {"start": v(498.77, -1449.4) * mm, "mid": v(498.99, -1449.35) * mm, "end": v(499.11, -1449.52) * mm});
            skArc(sketch, "E994", {"start": v(509.8, -1455.22) * mm, "mid": v(509.58, -1455.37) * mm, "end": v(509.63, -1455.64) * mm});
            skArc(sketch, "E995", {"start": v(515.74, -1444.57) * mm, "mid": v(515.53, -1444.62) * mm, "end": v(515.4, -1444.44) * mm});
            skArc(sketch, "E996", {"start": v(504.7, -1438.75) * mm, "mid": v(504.94, -1438.6) * mm, "end": v(504.89, -1438.32) * mm});
            skArc(sketch, "E997", {"start": v(515.66, -1438.18) * mm, "mid": v(515.92, -1438.33) * mm, "end": v(516.06, -1438.6) * mm});
            skArc(sketch, "E998", {"start": v(498.77, -1444.57) * mm, "mid": v(498.99, -1444.62) * mm, "end": v(499.11, -1444.44) * mm});
            skSolve(sketch);
        }
        {
            var Q0;
            Q0=makeQuery(id+"F29.imprint","IMPRINT",FACE,{"disambiguationData":[TD([[makeQuery(id+"F29.imprint","IMPRINT",EDGE,{"derivedFrom":sQuery(id+"F29.wireOp",EDGE,"E890")}),-1.0]])]});
            extrude(context, id + "F30", {"entities" : qUnion([Q0]), "depth" : 340 * mm});
        }
        {
            var Q0;
            Q0=makeQuery(id+"F29.imprint","IMPRINT",FACE,{"disambiguationData":[TD([[makeQuery(id+"F29.imprint","IMPRINT",EDGE,{"derivedFrom":sQuery(id+"F29.wireOp",EDGE,"E781")}),-1.0]])]});
            extrude(context, id + "F31", {"entities" : qUnion([Q0]), "depth" : 340 * mm});
        }
        {
            var Q0;
            Q0=makeQuery(id+"F29.imprint","IMPRINT",FACE,{"disambiguationData":[TD([[makeQuery(id+"F29.imprint","IMPRINT",EDGE,{"derivedFrom":sQuery(id+"F29.wireOp",EDGE,"E672")}),-1.0]])]});
            extrude(context, id + "F32", {"entities" : qUnion([Q0]), "depth" : 340 * mm});
        }
    });
